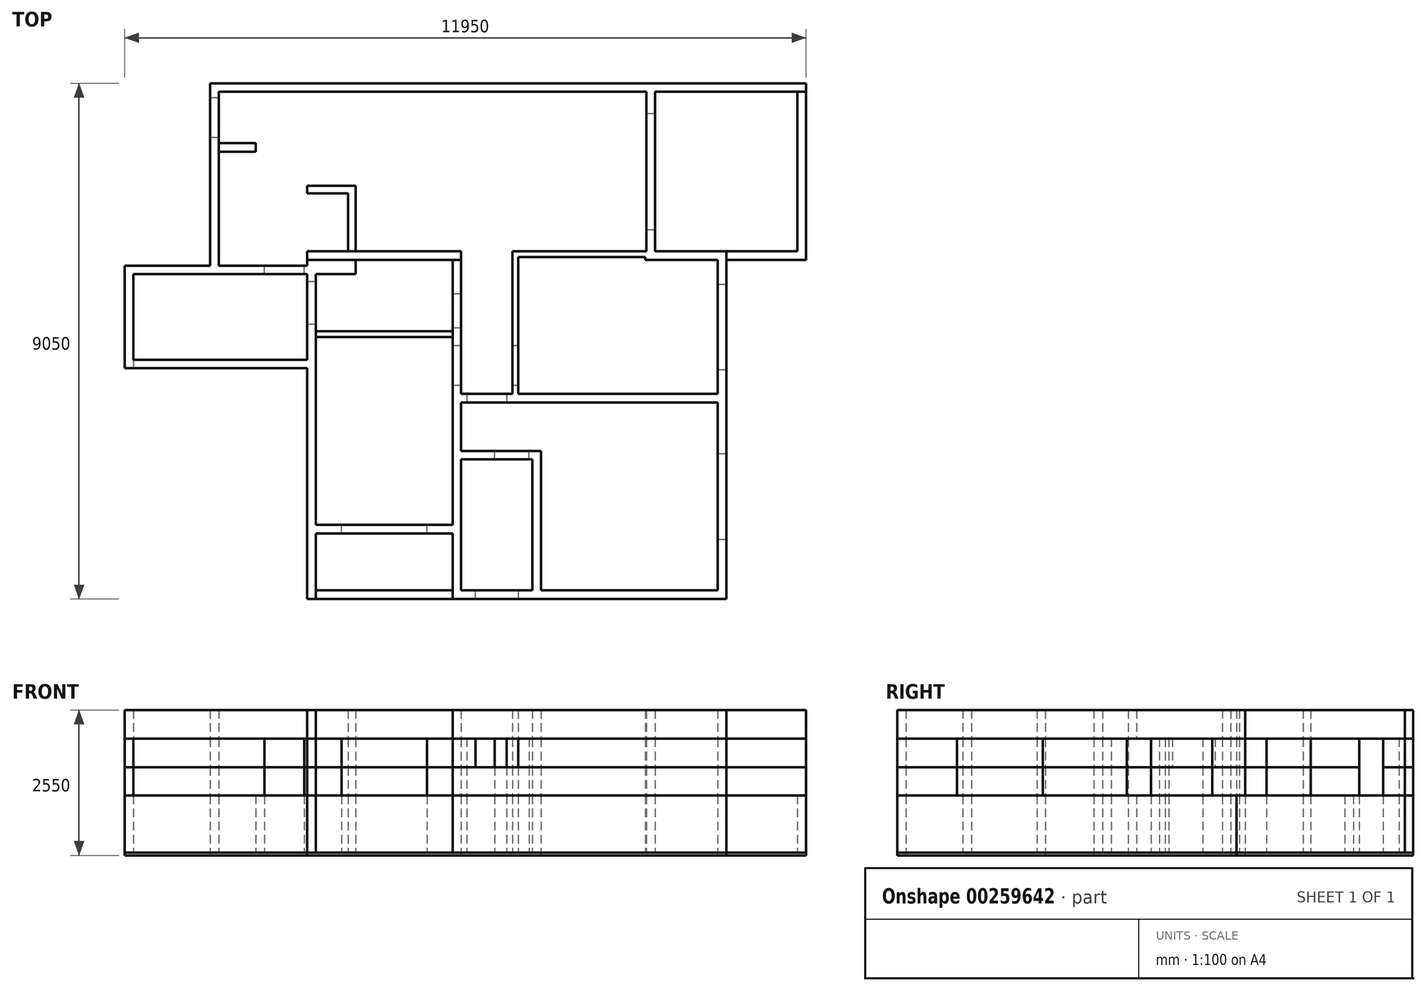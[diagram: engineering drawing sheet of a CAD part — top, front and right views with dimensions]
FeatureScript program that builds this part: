
annotation { "Feature Type Name" : "Feature", "Feature Type Description" : "" }
export const myFeature = defineFeature(function(context is Context, id is Id, definition is map)
    precondition{}
    {
        {
            var Q0;
            Q0=qCreatedBy(makeId("Top.planeOp"),FACE);
            var sketch = newSketch(context, id + "F0", { "sketchPlane" : qUnion([Q0])});
            skLineSegment(sketch, "E0.bottom", {"start": v(-5150, 2800) * mm, "end": v(2350, 2800) * mm});
            skLineSegment(sketch, "E0.top", {"start": v(-3600, 0) * mm, "end": v(-900, 0) * mm});
            skLineSegment(sketch, "E0.left", {"start": v(-5150, 2800) * mm, "end": v(-5150, 0) * mm});
            skLineSegment(sketch, "E0.right", {"start": v(5000, 2800) * mm, "end": v(5000, 0) * mm});
            skLineSegment(sketch, "E1.bottom", {"start": v(-5300, 2950) * mm, "end": v(5150, 2950) * mm});
            skLineSegment(sketch, "E1.top", {"start": v(-5300, -150) * mm, "end": v(-5150, -150) * mm});
            skLineSegment(sketch, "E1.left", {"start": v(-5300, 2950) * mm, "end": v(-5300, -150) * mm});
            skLineSegment(sketch, "E1.right", {"start": v(5150, 2950) * mm, "end": v(5150, -150) * mm});
            skLineSegment(sketch, "E2.top", {"start": v(2350, 2420) * mm, "end": v(2500, 2420) * mm});
            skLineSegment(sketch, "E2.left", {"start": v(2350, 2800) * mm, "end": v(2350, 2420) * mm});
            skLineSegment(sketch, "E2.right", {"start": v(2500, 2800) * mm, "end": v(2500, 2420) * mm});
            skLineSegment(sketch, "E3.top", {"start": v(2350, 380) * mm, "end": v(2500, 380) * mm});
            skLineSegment(sketch, "E3.left", {"start": v(2350, 2420) * mm, "end": v(2350, 380) * mm});
            skLineSegment(sketch, "E3.right", {"start": v(2500, 2420) * mm, "end": v(2500, 380) * mm});
            skLineSegment(sketch, "E4.left", {"start": v(2350, 380) * mm, "end": v(2350, 0) * mm});
            skLineSegment(sketch, "E4.right", {"start": v(2500, 380) * mm, "end": v(2500, 0) * mm});
            skLineSegment(sketch, "E5.bottom", {"start": v(0, 0) * mm, "end": v(2350, 0) * mm});
            skLineSegment(sketch, "E5.top", {"start": v(0, -2650) * mm, "end": v(3600, -2650) * mm});
            skLineSegment(sketch, "E5.left", {"start": v(0, 0) * mm, "end": v(0, -2650) * mm});
            skLineSegment(sketch, "E5.right", {"start": v(3750, 0) * mm, "end": v(3750, -2650) * mm});
            skLineSegment(sketch, "E6.bottom", {"start": v(100, -2500) * mm, "end": v(3600, -2500) * mm});
            skLineSegment(sketch, "E6.top", {"start": v(100, -100) * mm, "end": v(2330, -100) * mm});
            skLineSegment(sketch, "E6.left", {"start": v(100, -2500) * mm, "end": v(100, -100) * mm});
            skLineSegment(sketch, "E6.right", {"start": v(3600, -2500) * mm, "end": v(3600, -150) * mm});
            skLineSegment(sketch, "E7", {"start": v(2330, -100) * mm, "end": v(2330, -150) * mm});
            skLineSegment(sketch, "E8.trimOffspring", {"start": v(2330, -150) * mm, "end": v(3600, -150) * mm});
            skLineSegment(sketch, "E9.trimOffspring", {"start": v(2500, 2800) * mm, "end": v(5000, 2800) * mm});
            skLineSegment(sketch, "E10.trimOffspring", {"start": v(2500, 0) * mm, "end": v(3750, 0) * mm});
            skLineSegment(sketch, "E11.trimOffspring", {"start": v(2500, 0) * mm, "end": v(5000, 0) * mm});
            skLineSegment(sketch, "E12.trimOffspring", {"start": v(3750, -150) * mm, "end": v(5150, -150) * mm});
            skLineSegment(sketch, "E13.bottom", {"start": v(3600, -2500) * mm, "end": v(-1050, -2500) * mm});
            skLineSegment(sketch, "E13.top", {"start": v(3750, -6100) * mm, "end": v(-1050, -6100) * mm});
            skLineSegment(sketch, "E13.left", {"start": v(3750, -2500) * mm, "end": v(3750, -6100) * mm});
            skLineSegment(sketch, "E13.right", {"start": v(-1050, -2500) * mm, "end": v(-1050, -4800) * mm});
            skLineSegment(sketch, "E14.bottom", {"start": v(3600, -2650) * mm, "end": v(-900, -2650) * mm});
            skLineSegment(sketch, "E14.top", {"start": v(3600, -5950) * mm, "end": v(-900, -5950) * mm});
            skLineSegment(sketch, "E14.left", {"start": v(3600, -2650) * mm, "end": v(3600, -5950) * mm});
            skLineSegment(sketch, "E14.right", {"start": v(-900, -2650) * mm, "end": v(-900, -5950) * mm});
            skLineSegment(sketch, "E15.bottom", {"start": v(-900, -6100) * mm, "end": v(-3600, -6100) * mm});
            skLineSegment(sketch, "E15.top", {"start": v(-900, 0) * mm, "end": v(-3600, 0) * mm});
            skLineSegment(sketch, "E15.left", {"start": v(-900, -6100) * mm, "end": v(-900, 0) * mm});
            skLineSegment(sketch, "E15.right", {"start": v(-3600, -6100) * mm, "end": v(-3600, 0) * mm});
            skLineSegment(sketch, "E16.bottom", {"start": v(-1050, -5950) * mm, "end": v(-3450, -5950) * mm});
            skLineSegment(sketch, "E16.top", {"start": v(-1050, -150) * mm, "end": v(-3450, -150) * mm});
            skLineSegment(sketch, "E16.left", {"start": v(-1050, -5950) * mm, "end": v(-1050, -4950) * mm});
            skLineSegment(sketch, "E16.right", {"start": v(-3450, -5950) * mm, "end": v(-3450, -4950) * mm});
            skLineSegment(sketch, "E17.bottom", {"start": v(-1050, -1400) * mm, "end": v(-3450, -1400) * mm});
            skLineSegment(sketch, "E17.top", {"start": v(-1050, -1500) * mm, "end": v(-3450, -1500) * mm});
            skLineSegment(sketch, "E17.left", {"start": v(-1050, -1400) * mm, "end": v(-1050, -1500) * mm});
            skLineSegment(sketch, "E17.right", {"start": v(-3450, -1400) * mm, "end": v(-3450, -1500) * mm});
            skLineSegment(sketch, "E18.bottom", {"start": v(-3450, -4950) * mm, "end": v(-3000, -4950) * mm});
            skLineSegment(sketch, "E18.top", {"start": v(-3450, -4800) * mm, "end": v(-3000, -4800) * mm});
            skLineSegment(sketch, "E18.right", {"start": v(-3000, -4950) * mm, "end": v(-3000, -4800) * mm});
            skLineSegment(sketch, "E19.bottom", {"start": v(-3000, -4950) * mm, "end": v(-1500, -4950) * mm});
            skLineSegment(sketch, "E19.top", {"start": v(-3000, -4800) * mm, "end": v(-1500, -4800) * mm});
            skLineSegment(sketch, "E19.right", {"start": v(-1500, -4950) * mm, "end": v(-1500, -4800) * mm});
            skLineSegment(sketch, "E20.bottom", {"start": v(-1500, -4950) * mm, "end": v(-1050, -4950) * mm});
            skLineSegment(sketch, "E20.top", {"start": v(-1500, -4800) * mm, "end": v(-1050, -4800) * mm});
            skLineSegment(sketch, "E21.trimOffspring", {"start": v(-3450, -4800) * mm, "end": v(-3450, -150) * mm});
            skLineSegment(sketch, "E22.trimOffspring", {"start": v(-1050, -4950) * mm, "end": v(-1050, -6100) * mm});
            skLineSegment(sketch, "E23.trimOffspring", {"start": v(-1050, -4800) * mm, "end": v(-1050, -150) * mm});
            skLineSegment(sketch, "E24.trimOffspring", {"start": v(0, -150) * mm, "end": v(100, -150) * mm});
            skLineSegment(sketch, "E25.bottom", {"start": v(-5150, 1750) * mm, "end": v(-4500, 1750) * mm});
            skLineSegment(sketch, "E25.top", {"start": v(-5150, -250) * mm, "end": v(-2750, -250) * mm});
            skLineSegment(sketch, "E25.left", {"start": v(-5150, 1750) * mm, "end": v(-5150, -250) * mm});
            skLineSegment(sketch, "E25.right", {"start": v(-2750, 1750) * mm, "end": v(-2750, -250) * mm});
            skLineSegment(sketch, "E26.bottom", {"start": v(-5300, 1900) * mm, "end": v(-2750, 1900) * mm});
            skLineSegment(sketch, "E26.top", {"start": v(-5300, -400) * mm, "end": v(-2750, -400) * mm});
            skLineSegment(sketch, "E26.left", {"start": v(-5300, 1900) * mm, "end": v(-5300, -400) * mm});
            skLineSegment(sketch, "E26.right", {"start": v(-2750, 1900) * mm, "end": v(-2750, -400) * mm});
            skLineSegment(sketch, "E27", {"start": v(-4500, 1750) * mm, "end": v(-4500, 1900) * mm});
            skLineSegment(sketch, "E28.trimOffspring", {"start": v(-3600, -150) * mm, "end": v(-900, -150) * mm});
            skLineSegment(sketch, "E29.bottom", {"start": v(-3600, -400) * mm, "end": v(-6650, -400) * mm});
            skLineSegment(sketch, "E29.top", {"start": v(-3600, -1900) * mm, "end": v(-6650, -1900) * mm});
            skLineSegment(sketch, "E29.left", {"start": v(-3600, -400) * mm, "end": v(-3600, -1900) * mm});
            skLineSegment(sketch, "E29.right", {"start": v(-6650, -400) * mm, "end": v(-6650, -1900) * mm});
            skLineSegment(sketch, "E30.bottom", {"start": v(-3600, -400) * mm, "end": v(-6800, -400) * mm});
            skLineSegment(sketch, "E30.top", {"start": v(-3600, -2050) * mm, "end": v(-6800, -2050) * mm});
            skLineSegment(sketch, "E30.left", {"start": v(-3600, -400) * mm, "end": v(-3600, -2050) * mm});
            skLineSegment(sketch, "E30.right", {"start": v(-6800, -400) * mm, "end": v(-6800, -2050) * mm});
            skLineSegment(sketch, "E31", {"start": v(-2750, 1150) * mm, "end": v(-3600, 1150) * mm});
            skLineSegment(sketch, "E32", {"start": v(-3600, 1150) * mm, "end": v(-3600, 1020) * mm});
            skLineSegment(sketch, "E33", {"start": v(-3600, 1020) * mm, "end": v(-2880, 1020) * mm});
            skLineSegment(sketch, "E34", {"start": v(-2880, 1020) * mm, "end": v(-2880, 0) * mm});
            skLineSegment(sketch, "E35.bottom", {"start": v(-900, -5950) * mm, "end": v(350, -5950) * mm});
            skLineSegment(sketch, "E35.top", {"start": v(-900, -3650) * mm, "end": v(350, -3650) * mm});
            skLineSegment(sketch, "E35.left", {"start": v(-900, -5950) * mm, "end": v(-900, -3650) * mm});
            skLineSegment(sketch, "E35.right", {"start": v(350, -5950) * mm, "end": v(350, -3650) * mm});
            skLineSegment(sketch, "E36.bottom", {"start": v(-900, -5950) * mm, "end": v(500, -5950) * mm});
            skLineSegment(sketch, "E36.top", {"start": v(-900, -3500) * mm, "end": v(500, -3500) * mm});
            skLineSegment(sketch, "E36.left", {"start": v(-900, -5950) * mm, "end": v(-900, -3500) * mm});
            skLineSegment(sketch, "E36.right", {"start": v(500, -5950) * mm, "end": v(500, -3500) * mm});
            skLineSegment(sketch, "E37", {"start": v(2350, 0) * mm, "end": v(2350, -150) * mm});
            skLineSegment(sketch, "E38", {"start": v(5000, 2800) * mm, "end": v(5150, 2800) * mm});
            skLineSegment(sketch, "E39.bottom", {"start": v(-6800, -400) * mm, "end": v(-5300, -400) * mm});
            skLineSegment(sketch, "E39.top", {"start": v(-6800, -250) * mm, "end": v(-5300, -250) * mm});
            skLineSegment(sketch, "E39.left", {"start": v(-6800, -400) * mm, "end": v(-6800, -250) * mm});
            skLineSegment(sketch, "E39.right", {"start": v(-5300, -400) * mm, "end": v(-5300, -250) * mm});
            skLineSegment(sketch, "E40", {"start": v(-3450, -5950) * mm, "end": v(-3450, -6100) * mm});
            skLineSegment(sketch, "E41", {"start": v(-6650, -1900) * mm, "end": v(-6650, -2050) * mm});
            skLineSegment(sketch, "E42", {"start": v(3600, -5050) * mm, "end": v(3750, -5050) * mm});
            skLineSegment(sketch, "E43", {"start": v(3600, -3550) * mm, "end": v(3750, -3550) * mm});
            skLineSegment(sketch, "E44", {"start": v(3600, -575) * mm, "end": v(3750, -575) * mm});
            skLineSegment(sketch, "E45", {"start": v(3600, -2075) * mm, "end": v(3750, -2075) * mm});
            skLineSegment(sketch, "E46", {"start": v(3600, -4300) * mm, "end": v(3750, -4300) * mm, "construction": true});
            skLineSegment(sketch, "E47", {"start": v(3600, -1325) * mm, "end": v(3750, -1325) * mm, "construction": true});
            skLineSegment(sketch, "E48", {"start": v(-800, -2500) * mm, "end": v(-800, -2650) * mm});
            skLineSegment(sketch, "E49", {"start": v(-100, -2500) * mm, "end": v(-100, -2650) * mm});
            skLineSegment(sketch, "E50", {"start": v(-450, -2500) * mm, "end": v(-450, -2650) * mm, "construction": true});
            skLineSegment(sketch, "E51", {"start": v(290, -3650) * mm, "end": v(290, -3500) * mm});
            skLineSegment(sketch, "E52", {"start": v(-310, -3650) * mm, "end": v(-310, -3500) * mm});
            skLineSegment(sketch, "E53", {"start": v(-1050, -1650) * mm, "end": v(-900, -1650) * mm});
            skLineSegment(sketch, "E54", {"start": v(-1050, -2350) * mm, "end": v(-900, -2350) * mm});
            skLineSegment(sketch, "E55", {"start": v(-1050, -1340) * mm, "end": v(-900, -1340) * mm});
            skLineSegment(sketch, "E56", {"start": v(-1050, -740) * mm, "end": v(-900, -740) * mm});
            skLineSegment(sketch, "E57", {"start": v(-3600, -525) * mm, "end": v(-3450, -525) * mm});
            skLineSegment(sketch, "E58", {"start": v(-3600, -1275) * mm, "end": v(-3450, -1275) * mm});
            skLineSegment(sketch, "E59", {"start": v(-650, -6100) * mm, "end": v(-650, -5950) * mm});
            skLineSegment(sketch, "E60", {"start": v(-3600, -900) * mm, "end": v(-3450, -900) * mm, "construction": true});
            skLineSegment(sketch, "E61", {"start": v(-275, -5950) * mm, "end": v(-275, -6100) * mm, "construction": true});
            skLineSegment(sketch, "E62", {"start": v(100, -5950) * mm, "end": v(100, -6100) * mm});
            skLineSegment(sketch, "E63", {"start": v(-5300, 2000) * mm, "end": v(-5150, 2000) * mm});
            skLineSegment(sketch, "E64", {"start": v(-5300, 2700) * mm, "end": v(-5150, 2700) * mm});
            skLineSegment(sketch, "E65", {"start": v(-5300, 2350) * mm, "end": v(-5150, 2350) * mm, "construction": true});
            skLineSegment(sketch, "E66", {"start": v(0, -2350) * mm, "end": v(100, -2350) * mm});
            skLineSegment(sketch, "E67", {"start": v(0, -1650) * mm, "end": v(100, -1650) * mm});
            skLineSegment(sketch, "E68", {"start": v(-3650, -400) * mm, "end": v(-3650, -250) * mm});
            skLineSegment(sketch, "E69", {"start": v(-4350, -400) * mm, "end": v(-4350, -250) * mm});
            skLineSegment(sketch, "E70", {"start": v(-1050, -2000) * mm, "end": v(-900, -2000) * mm, "construction": true});
            skSolve(sketch);
        }
        {
            var Q0;
            {var subQ1=sQuery(id+"F0.wireOp",EDGE,"E14.top");Q0=makeQuery(id+"F0.imprint","IMPRINT",FACE,{"disambiguationData":[TD([[makeQuery(id+"F0.imprint","IMPRINT",EDGE,{"derivedFrom":subQ1}),1.0]])]});}
            var Q1;
            {var subQ0=sQuery(id+"F0.wireOp",EDGE,"E42");Q1=makeQuery(id+"F0.imprint","IMPRINT",FACE,{"disambiguationData":[TD([[makeQuery(id+"F0.imprint","IMPRINT",EDGE,{"derivedFrom":subQ0}),1.0]])]});}
            var Q2;
            {var subQ7=sQuery(id+"F0.wireOp",EDGE,"E43");Q2=makeQuery(id+"F0.imprint","IMPRINT",FACE,{"disambiguationData":[TD([[makeQuery(id+"F0.imprint","IMPRINT",EDGE,{"derivedFrom":subQ7}),1.0]])]});}
            var Q3;
            {var subQ1=sQuery(id+"F0.wireOp",EDGE,"E14.top");Q3=makeQuery(id+"F0.imprint","IMPRINT",FACE,{"disambiguationData":[TD([[makeQuery(id+"F0.imprint","IMPRINT",EDGE,{"derivedFrom":subQ1}),-1.0]])]});}
            var Q4;
            {var subQ3=sQuery(id+"F0.wireOp",EDGE,"E35.right");Q4=makeQuery(id+"F0.imprint","IMPRINT",FACE,{"disambiguationData":[TD([[makeQuery(id+"F0.imprint","IMPRINT",EDGE,{"derivedFrom":subQ3}),-1.0]])]});}
            var Q5;
            {var subQ0=sQuery(id+"F0.wireOp",EDGE,"E51");Q5=makeQuery(id+"F0.imprint","IMPRINT",FACE,{"disambiguationData":[TD([[makeQuery(id+"F0.imprint","IMPRINT",EDGE,{"derivedFrom":subQ0}),1.0]])]});}
            var Q6;
            {var subQ3=sQuery(id+"F0.wireOp",EDGE,"E52");Q6=makeQuery(id+"F0.imprint","IMPRINT",FACE,{"disambiguationData":[TD([[makeQuery(id+"F0.imprint","IMPRINT",EDGE,{"derivedFrom":subQ3}),1.0]])]});}
            var Q7;
            {var subQ0=sQuery(id+"F0.wireOp",EDGE,"E59");Q7=makeQuery(id+"F0.imprint","IMPRINT",FACE,{"disambiguationData":[TD([[makeQuery(id+"F0.imprint","IMPRINT",EDGE,{"derivedFrom":subQ0}),-1.0]])]});}
            var Q8;
            {var subQ3=sQuery(id+"F0.wireOp",EDGE,"E59");Q8=makeQuery(id+"F0.imprint","IMPRINT",FACE,{"disambiguationData":[TD([[makeQuery(id+"F0.imprint","IMPRINT",EDGE,{"derivedFrom":subQ3}),1.0]])]});}
            var Q9;
            {var subQ2=sQuery(id+"F0.wireOp",EDGE,"E20.bottom");Q9=makeQuery(id+"F0.imprint","IMPRINT",FACE,{"disambiguationData":[TD([[makeQuery(id+"F0.imprint","IMPRINT",EDGE,{"derivedFrom":subQ2}),1.0]])]});}
            var Q10;
            Q10=makeQuery(id+"F0.imprint","IMPRINT",FACE,{"disambiguationData":[TD([[makeQuery(id+"F0.imprint","IMPRINT",EDGE,{"derivedFrom":sQuery(id+"F0.wireOp",EDGE,"E19.bottom")}),1.0]])]});
            var Q11;
            Q11=makeQuery(id+"F0.imprint","IMPRINT",FACE,{"disambiguationData":[TD([[makeQuery(id+"F0.imprint","IMPRINT",EDGE,{"derivedFrom":sQuery(id+"F0.wireOp",EDGE,"E16.right")}),1.0]])]});
            var Q12;
            {var subQ4=sQuery(id+"F0.wireOp",EDGE,"E17.top");Q12=makeQuery(id+"F0.imprint","IMPRINT",FACE,{"disambiguationData":[TD([[makeQuery(id+"F0.imprint","IMPRINT",EDGE,{"derivedFrom":subQ4}),1.0]])]});}
            var Q13;
            {var subQ5=sQuery(id+"F0.wireOp",EDGE,"E54");Q13=makeQuery(id+"F0.imprint","IMPRINT",FACE,{"disambiguationData":[TD([[makeQuery(id+"F0.imprint","IMPRINT",EDGE,{"derivedFrom":subQ5}),-1.0]])]});}
            var Q14;
            {var subQ0=sQuery(id+"F0.wireOp",EDGE,"E48");Q14=makeQuery(id+"F0.imprint","IMPRINT",FACE,{"disambiguationData":[TD([[makeQuery(id+"F0.imprint","IMPRINT",EDGE,{"derivedFrom":subQ0}),-1.0]])]});}
            var Q15;
            {var subQ0=sQuery(id+"F0.wireOp",EDGE,"E48");Q15=makeQuery(id+"F0.imprint","IMPRINT",FACE,{"disambiguationData":[TD([[makeQuery(id+"F0.imprint","IMPRINT",EDGE,{"derivedFrom":subQ0}),1.0]])]});}
            var Q16;
            {var subQ5=sQuery(id+"F0.wireOp",EDGE,"E49");Q16=makeQuery(id+"F0.imprint","IMPRINT",FACE,{"disambiguationData":[TD([[makeQuery(id+"F0.imprint","IMPRINT",EDGE,{"derivedFrom":subQ5}),1.0]])]});}
            var Q17;
            {var subQ0=sQuery(id+"F0.wireOp",EDGE,"E53");Q17=makeQuery(id+"F0.imprint","IMPRINT",FACE,{"disambiguationData":[TD([[makeQuery(id+"F0.imprint","IMPRINT",EDGE,{"derivedFrom":subQ0}),-1.0]])]});}
            var Q18;
            {var subQ4=sQuery(id+"F0.wireOp",EDGE,"E53");Q18=makeQuery(id+"F0.imprint","IMPRINT",FACE,{"disambiguationData":[TD([[makeQuery(id+"F0.imprint","IMPRINT",EDGE,{"derivedFrom":subQ4}),1.0]])]});}
            var Q19;
            {var subQ0=sQuery(id+"F0.wireOp",EDGE,"E55");Q19=makeQuery(id+"F0.imprint","IMPRINT",FACE,{"disambiguationData":[TD([[makeQuery(id+"F0.imprint","IMPRINT",EDGE,{"derivedFrom":subQ0}),1.0]])]});}
            var Q20;
            {var subQ0=sQuery(id+"F0.wireOp",EDGE,"E17.bottom");Q20=makeQuery(id+"F0.imprint","IMPRINT",FACE,{"disambiguationData":[TD([[makeQuery(id+"F0.imprint","IMPRINT",EDGE,{"derivedFrom":subQ0}),1.0]])]});}
            var Q21;
            {var subQ3=sQuery(id+"F0.wireOp",EDGE,"E56");Q21=makeQuery(id+"F0.imprint","IMPRINT",FACE,{"disambiguationData":[TD([[makeQuery(id+"F0.imprint","IMPRINT",EDGE,{"derivedFrom":subQ3}),1.0]])]});}
            var Q22;
            {var subQ1=sQuery(id+"F0.wireOp",EDGE,"E15.top");var subQ5=sQuery(id+"F0.wireOp",EDGE,"E15.left");var subQ6=makeQuery(id+"F0.imprint","INTERSECT",VERTEX,{"derivedFrom":[subQ1,subQ5]});Q22=makeQuery(id+"F0.imprint","IMPRINT",FACE,{"disambiguationData":[TD([[makeQuery(id+"F0.imprint","IMPRINT",EDGE,{"disambiguationData":[TD([[subQ6,-1.0]])],"derivedFrom":subQ1}),1.0]])]});}
            var Q23;
            {var subQ0=sQuery(id+"F0.wireOp",EDGE,"E57");Q23=makeQuery(id+"F0.imprint","IMPRINT",FACE,{"disambiguationData":[TD([[makeQuery(id+"F0.imprint","IMPRINT",EDGE,{"derivedFrom":subQ0}),-1.0]])]});}
            var Q24;
            {var subQ0=sQuery(id+"F0.wireOp",EDGE,"E57");Q24=makeQuery(id+"F0.imprint","IMPRINT",FACE,{"disambiguationData":[TD([[makeQuery(id+"F0.imprint","IMPRINT",EDGE,{"derivedFrom":subQ0}),1.0]])]});}
            var Q25;
            {var subQ0=sQuery(id+"F0.wireOp",EDGE,"E26.top");var subQ5=sQuery(id+"F0.wireOp",EDGE,"E21.trimOffspring");var subQ6=makeQuery(id+"F0.imprint","INTERSECT",VERTEX,{"derivedFrom":[subQ5,subQ0]});Q25=makeQuery(id+"F0.imprint","IMPRINT",FACE,{"disambiguationData":[TD([[makeQuery(id+"F0.imprint","IMPRINT",EDGE,{"disambiguationData":[TD([[subQ6,-1.0]])],"derivedFrom":subQ5}),1.0]])]});}
            var Q26;
            {var subQ0=sQuery(id+"F0.wireOp",EDGE,"E26.top");var subQ1=sQuery(id+"F0.wireOp",EDGE,"E21.trimOffspring");var subQ2=makeQuery(id+"F0.imprint","INTERSECT",VERTEX,{"derivedFrom":[subQ1,subQ0]});Q26=makeQuery(id+"F0.imprint","IMPRINT",FACE,{"disambiguationData":[TD([[makeQuery(id+"F0.imprint","IMPRINT",EDGE,{"disambiguationData":[TD([[subQ2,-1.0]])],"derivedFrom":subQ1}),-1.0]])]});}
            var Q27;
            {var subQ0=sQuery(id+"F0.wireOp",EDGE,"E28.trimOffspring");var subQ1=sQuery(id+"F0.wireOp",EDGE,"E21.trimOffspring");var subQ2=makeQuery(id+"F0.imprint","INTERSECT",VERTEX,{"derivedFrom":[subQ1,subQ0]});Q27=makeQuery(id+"F0.imprint","IMPRINT",FACE,{"disambiguationData":[TD([[makeQuery(id+"F0.imprint","IMPRINT",EDGE,{"disambiguationData":[TD([[subQ2,1.0]])],"derivedFrom":subQ1}),-1.0]])]});}
            var Q28;
            {var subQ1=sQuery(id+"F0.wireOp",EDGE,"E15.top");var subQ8=makeQuery(id+"F0.imprint","INTERSECT",VERTEX,{"derivedFrom":[subQ1,sQuery(id+"F0.wireOp",EDGE,"E34")]});Q28=makeQuery(id+"F0.imprint","IMPRINT",FACE,{"disambiguationData":[TD([[makeQuery(id+"F0.imprint","IMPRINT",EDGE,{"disambiguationData":[TD([[subQ8,1.0]])],"derivedFrom":subQ1}),1.0]])]});}
            var Q29;
            {var subQ0=sQuery(id+"F0.wireOp",EDGE,"E28.trimOffspring");var subQ1=sQuery(id+"F0.wireOp",EDGE,"E15.right");var subQ2=makeQuery(id+"F0.imprint","INTERSECT",VERTEX,{"derivedFrom":[subQ1,subQ0]});Q29=makeQuery(id+"F0.imprint","IMPRINT",FACE,{"disambiguationData":[TD([[makeQuery(id+"F0.imprint","IMPRINT",EDGE,{"disambiguationData":[TD([[subQ2,1.0]])],"derivedFrom":subQ1}),-1.0]])]});}
            var Q30;
            {var subQ1=sQuery(id+"F0.wireOp",EDGE,"E1.top");Q30=makeQuery(id+"F0.imprint","IMPRINT",FACE,{"disambiguationData":[TD([[makeQuery(id+"F0.imprint","IMPRINT",EDGE,{"derivedFrom":subQ1}),-1.0]])]});}
            var Q31;
            Q31=makeQuery(id+"F0.imprint","IMPRINT",FACE,{"disambiguationData":[TD([[makeQuery(id+"F0.imprint","IMPRINT",EDGE,{"derivedFrom":sQuery(id+"F0.wireOp",EDGE,"E39.top")}),-1.0]])]});
            var Q32;
            {var subQ1=sQuery(id+"F0.wireOp",EDGE,"E29.right");Q32=makeQuery(id+"F0.imprint","IMPRINT",FACE,{"disambiguationData":[TD([[makeQuery(id+"F0.imprint","IMPRINT",EDGE,{"derivedFrom":subQ1}),-1.0]])]});}
            var Q33;
            {var subQ1=sQuery(id+"F0.wireOp",EDGE,"E1.top");Q33=makeQuery(id+"F0.imprint","IMPRINT",FACE,{"disambiguationData":[TD([[makeQuery(id+"F0.imprint","IMPRINT",EDGE,{"derivedFrom":subQ1}),1.0]])]});}
            var Q34;
            {var subQ0=sQuery(id+"F0.wireOp",EDGE,"E63");Q34=makeQuery(id+"F0.imprint","IMPRINT",FACE,{"disambiguationData":[TD([[makeQuery(id+"F0.imprint","IMPRINT",EDGE,{"derivedFrom":subQ0}),-1.0]])]});}
            var Q35;
            {var subQ0=sQuery(id+"F0.wireOp",EDGE,"E63");Q35=makeQuery(id+"F0.imprint","IMPRINT",FACE,{"disambiguationData":[TD([[makeQuery(id+"F0.imprint","IMPRINT",EDGE,{"derivedFrom":subQ0}),1.0]])]});}
            var Q36;
            {var subQ5=sQuery(id+"F0.wireOp",EDGE,"E0.bottom");Q36=makeQuery(id+"F0.imprint","IMPRINT",FACE,{"disambiguationData":[TD([[makeQuery(id+"F0.imprint","IMPRINT",EDGE,{"derivedFrom":subQ5}),1.0]])]});}
            var Q37;
            Q37=makeQuery(id+"F0.imprint","IMPRINT",FACE,{"disambiguationData":[TD([[makeQuery(id+"F0.imprint","IMPRINT",EDGE,{"derivedFrom":sQuery(id+"F0.wireOp",EDGE,"E2.top")}),-1.0]])]});
            var Q38;
            {var subQ0=sQuery(id+"F0.wireOp",EDGE,"E44");Q38=makeQuery(id+"F0.imprint","IMPRINT",FACE,{"disambiguationData":[TD([[makeQuery(id+"F0.imprint","IMPRINT",EDGE,{"derivedFrom":subQ0}),-1.0]])]});}
            var Q39;
            Q39=makeQuery(id+"F0.imprint","IMPRINT",FACE,{"disambiguationData":[TD([[makeQuery(id+"F0.imprint","IMPRINT",EDGE,{"derivedFrom":sQuery(id+"F0.wireOp",EDGE,"E3.top")}),-1.0]])]});
            var Q40;
            {var subQ0=sQuery(id+"F0.wireOp",EDGE,"E35.right");Q40=makeQuery(id+"F0.imprint","IMPRINT",FACE,{"disambiguationData":[TD([[makeQuery(id+"F0.imprint","IMPRINT",EDGE,{"derivedFrom":subQ0}),1.0]])]});}
            var Q41;
            {var subQ0=sQuery(id+"F0.wireOp",EDGE,"E16.bottom");Q41=makeQuery(id+"F0.imprint","IMPRINT",FACE,{"disambiguationData":[TD([[makeQuery(id+"F0.imprint","IMPRINT",EDGE,{"derivedFrom":subQ0}),-1.0]])]});}
            var Q42;
            {var subQ4=sQuery(id+"F0.wireOp",EDGE,"E16.bottom");Q42=makeQuery(id+"F0.imprint","IMPRINT",FACE,{"disambiguationData":[TD([[makeQuery(id+"F0.imprint","IMPRINT",EDGE,{"derivedFrom":subQ4}),1.0]])]});}
            var Q43;
            {var subQ4=sQuery(id+"F0.wireOp",EDGE,"E29.top");Q43=makeQuery(id+"F0.imprint","IMPRINT",FACE,{"disambiguationData":[TD([[makeQuery(id+"F0.imprint","IMPRINT",EDGE,{"derivedFrom":subQ4}),-1.0]])]});}
            var Q44;
            {var subQ0=sQuery(id+"F0.wireOp",EDGE,"E29.top");Q44=makeQuery(id+"F0.imprint","IMPRINT",FACE,{"disambiguationData":[TD([[makeQuery(id+"F0.imprint","IMPRINT",EDGE,{"derivedFrom":subQ0}),1.0]])]});}
            var Q45;
            {var subQ11=sQuery(id+"F0.wireOp",EDGE,"E17.bottom");Q45=makeQuery(id+"F0.imprint","IMPRINT",FACE,{"disambiguationData":[TD([[makeQuery(id+"F0.imprint","IMPRINT",EDGE,{"derivedFrom":subQ11}),-1.0]])]});}
            var Q46;
            {var subQ10=sQuery(id+"F0.wireOp",EDGE,"E6.top");Q46=makeQuery(id+"F0.imprint","IMPRINT",FACE,{"disambiguationData":[TD([[makeQuery(id+"F0.imprint","IMPRINT",EDGE,{"derivedFrom":subQ10}),-1.0]])]});}
            var Q47;
            {var subQ20=sQuery(id+"F0.wireOp",EDGE,"E0.bottom");Q47=makeQuery(id+"F0.imprint","IMPRINT",FACE,{"disambiguationData":[TD([[makeQuery(id+"F0.imprint","IMPRINT",EDGE,{"derivedFrom":subQ20}),-1.0]])]});}
            var Q48;
            {var subQ0=sQuery(id+"F0.wireOp",EDGE,"E66");Q48=makeQuery(id+"F0.imprint","IMPRINT",FACE,{"disambiguationData":[TD([[makeQuery(id+"F0.imprint","IMPRINT",EDGE,{"derivedFrom":subQ0}),-1.0]])]});}
            var Q49;
            {var subQ0=sQuery(id+"F0.wireOp",EDGE,"E66");Q49=makeQuery(id+"F0.imprint","IMPRINT",FACE,{"disambiguationData":[TD([[makeQuery(id+"F0.imprint","IMPRINT",EDGE,{"derivedFrom":subQ0}),1.0]])]});}
            var Q50;
            {var subQ0=sQuery(id+"F0.wireOp",EDGE,"E24.trimOffspring");Q50=makeQuery(id+"F0.imprint","IMPRINT",FACE,{"disambiguationData":[TD([[makeQuery(id+"F0.imprint","IMPRINT",EDGE,{"derivedFrom":subQ0}),-1.0]])]});}
            var Q51;
            {var subQ2=sQuery(id+"F0.wireOp",EDGE,"E6.top");Q51=makeQuery(id+"F0.imprint","IMPRINT",FACE,{"disambiguationData":[TD([[makeQuery(id+"F0.imprint","IMPRINT",EDGE,{"derivedFrom":subQ2}),1.0]])]});}
            var Q52;
            {var subQ3=sQuery(id+"F0.wireOp",EDGE,"E0.right");Q52=makeQuery(id+"F0.imprint","IMPRINT",FACE,{"disambiguationData":[TD([[makeQuery(id+"F0.imprint","IMPRINT",EDGE,{"derivedFrom":subQ3}),-1.0]])]});}
            var Q53;
            {var subQ1=sQuery(id+"F0.wireOp",EDGE,"E0.right");Q53=makeQuery(id+"F0.imprint","IMPRINT",FACE,{"disambiguationData":[TD([[makeQuery(id+"F0.imprint","IMPRINT",EDGE,{"derivedFrom":subQ1}),1.0]])]});}
            var Q54;
            {var subQ14=sQuery(id+"F0.wireOp",EDGE,"E25.bottom");Q54=makeQuery(id+"F0.imprint","IMPRINT",FACE,{"disambiguationData":[TD([[makeQuery(id+"F0.imprint","IMPRINT",EDGE,{"derivedFrom":subQ14}),-1.0]])]});}
            var Q55;
            {var subQ0=sQuery(id+"F0.wireOp",EDGE,"E25.bottom");Q55=makeQuery(id+"F0.imprint","IMPRINT",FACE,{"disambiguationData":[TD([[makeQuery(id+"F0.imprint","IMPRINT",EDGE,{"derivedFrom":subQ0}),1.0]])]});}
            var Q56;
            {var subQ0=sQuery(id+"F0.wireOp",EDGE,"E31");Q56=makeQuery(id+"F0.imprint","IMPRINT",FACE,{"disambiguationData":[TD([[makeQuery(id+"F0.imprint","IMPRINT",EDGE,{"derivedFrom":subQ0}),1.0]])]});}
            var Q57;
            {var subQ0=sQuery(id+"F0.wireOp",EDGE,"E68");Q57=makeQuery(id+"F0.imprint","IMPRINT",FACE,{"disambiguationData":[TD([[makeQuery(id+"F0.imprint","IMPRINT",EDGE,{"derivedFrom":subQ0}),1.0]])]});}
            var Q58;
            {var subQ5=sQuery(id+"F0.wireOp",EDGE,"E68");Q58=makeQuery(id+"F0.imprint","IMPRINT",FACE,{"disambiguationData":[TD([[makeQuery(id+"F0.imprint","IMPRINT",EDGE,{"derivedFrom":subQ5}),-1.0]])]});}
            extrude(context, id + "F1", {"entities" : qUnion([Q0, Q1, Q2, Q3, Q4, Q5, Q6, Q7, Q8, Q9, Q10, Q11, Q12, Q13, Q14, Q15, Q16, Q17, Q18, Q19, Q20, Q21, Q22, Q23, Q24, Q25, Q26, Q27, Q28, Q29, Q30, Q31, Q32, Q33, Q34, Q35, Q36, Q37, Q38, Q39, Q40, Q41, Q42, Q43, Q44, Q45, Q46, Q47, Q48, Q49, Q50, Q51, Q52, Q53, Q54, Q55, Q56, Q57, Q58]), "oppositeDirection" : true, "depth" : 50 * mm});
        }
        {
            var Q0;
            {var subQ1=sQuery(id+"F0.wireOp",EDGE,"E14.top");Q0=makeQuery(id+"F0.imprint","IMPRINT",FACE,{"disambiguationData":[TD([[makeQuery(id+"F0.imprint","IMPRINT",EDGE,{"derivedFrom":subQ1}),1.0]])]});}
            var Q1;
            {var subQ0=sQuery(id+"F0.wireOp",EDGE,"E42");Q1=makeQuery(id+"F0.imprint","IMPRINT",FACE,{"disambiguationData":[TD([[makeQuery(id+"F0.imprint","IMPRINT",EDGE,{"derivedFrom":subQ0}),1.0]])]});}
            var Q2;
            {var subQ7=sQuery(id+"F0.wireOp",EDGE,"E43");Q2=makeQuery(id+"F0.imprint","IMPRINT",FACE,{"disambiguationData":[TD([[makeQuery(id+"F0.imprint","IMPRINT",EDGE,{"derivedFrom":subQ7}),1.0]])]});}
            var Q3;
            {var subQ0=sQuery(id+"F0.wireOp",EDGE,"E44");Q3=makeQuery(id+"F0.imprint","IMPRINT",FACE,{"disambiguationData":[TD([[makeQuery(id+"F0.imprint","IMPRINT",EDGE,{"derivedFrom":subQ0}),-1.0]])]});}
            var Q4;
            Q4=makeQuery(id+"F0.imprint","IMPRINT",FACE,{"disambiguationData":[TD([[makeQuery(id+"F0.imprint","IMPRINT",EDGE,{"derivedFrom":sQuery(id+"F0.wireOp",EDGE,"E3.top")}),-1.0]])]});
            var Q5;
            {var subQ4=sQuery(id+"F0.wireOp",EDGE,"E0.bottom");Q5=makeQuery(id+"F0.imprint","IMPRINT",FACE,{"disambiguationData":[TD([[makeQuery(id+"F0.imprint","IMPRINT",EDGE,{"derivedFrom":subQ4}),1.0]])]});}
            var Q6;
            {var subQ3=sQuery(id+"F0.wireOp",EDGE,"E35.right");Q6=makeQuery(id+"F0.imprint","IMPRINT",FACE,{"disambiguationData":[TD([[makeQuery(id+"F0.imprint","IMPRINT",EDGE,{"derivedFrom":subQ3}),-1.0]])]});}
            var Q7;
            {var subQ3=sQuery(id+"F0.wireOp",EDGE,"E52");Q7=makeQuery(id+"F0.imprint","IMPRINT",FACE,{"disambiguationData":[TD([[makeQuery(id+"F0.imprint","IMPRINT",EDGE,{"derivedFrom":subQ3}),1.0]])]});}
            var Q8;
            {var subQ2=sQuery(id+"F0.wireOp",EDGE,"E20.bottom");Q8=makeQuery(id+"F0.imprint","IMPRINT",FACE,{"disambiguationData":[TD([[makeQuery(id+"F0.imprint","IMPRINT",EDGE,{"derivedFrom":subQ2}),1.0]])]});}
            var Q9;
            {var subQ0=sQuery(id+"F0.wireOp",EDGE,"E59");Q9=makeQuery(id+"F0.imprint","IMPRINT",FACE,{"disambiguationData":[TD([[makeQuery(id+"F0.imprint","IMPRINT",EDGE,{"derivedFrom":subQ0}),-1.0]])]});}
            var Q10;
            {var subQ3=sQuery(id+"F0.wireOp",EDGE,"E59");Q10=makeQuery(id+"F0.imprint","IMPRINT",FACE,{"disambiguationData":[TD([[makeQuery(id+"F0.imprint","IMPRINT",EDGE,{"derivedFrom":subQ3}),1.0]])]});}
            var Q11;
            Q11=makeQuery(id+"F0.imprint","IMPRINT",FACE,{"disambiguationData":[TD([[makeQuery(id+"F0.imprint","IMPRINT",EDGE,{"derivedFrom":sQuery(id+"F0.wireOp",EDGE,"E16.right")}),1.0]])]});
            var Q12;
            {var subQ0=sQuery(id+"F0.wireOp",EDGE,"E48");Q12=makeQuery(id+"F0.imprint","IMPRINT",FACE,{"disambiguationData":[TD([[makeQuery(id+"F0.imprint","IMPRINT",EDGE,{"derivedFrom":subQ0}),-1.0]])]});}
            var Q13;
            {var subQ5=sQuery(id+"F0.wireOp",EDGE,"E54");Q13=makeQuery(id+"F0.imprint","IMPRINT",FACE,{"disambiguationData":[TD([[makeQuery(id+"F0.imprint","IMPRINT",EDGE,{"derivedFrom":subQ5}),-1.0]])]});}
            var Q14;
            {var subQ4=sQuery(id+"F0.wireOp",EDGE,"E53");Q14=makeQuery(id+"F0.imprint","IMPRINT",FACE,{"disambiguationData":[TD([[makeQuery(id+"F0.imprint","IMPRINT",EDGE,{"derivedFrom":subQ4}),1.0]])]});}
            var Q15;
            {var subQ0=sQuery(id+"F0.wireOp",EDGE,"E17.bottom");Q15=makeQuery(id+"F0.imprint","IMPRINT",FACE,{"disambiguationData":[TD([[makeQuery(id+"F0.imprint","IMPRINT",EDGE,{"derivedFrom":subQ0}),1.0]])]});}
            var Q16;
            {var subQ0=sQuery(id+"F0.wireOp",EDGE,"E57");Q16=makeQuery(id+"F0.imprint","IMPRINT",FACE,{"disambiguationData":[TD([[makeQuery(id+"F0.imprint","IMPRINT",EDGE,{"derivedFrom":subQ0}),-1.0]])]});}
            var Q17;
            {var subQ0=sQuery(id+"F0.wireOp",EDGE,"E57");Q17=makeQuery(id+"F0.imprint","IMPRINT",FACE,{"disambiguationData":[TD([[makeQuery(id+"F0.imprint","IMPRINT",EDGE,{"derivedFrom":subQ0}),1.0]])]});}
            var Q18;
            {var subQ0=sQuery(id+"F0.wireOp",EDGE,"E26.top");var subQ5=sQuery(id+"F0.wireOp",EDGE,"E21.trimOffspring");var subQ6=makeQuery(id+"F0.imprint","INTERSECT",VERTEX,{"derivedFrom":[subQ5,subQ0]});Q18=makeQuery(id+"F0.imprint","IMPRINT",FACE,{"disambiguationData":[TD([[makeQuery(id+"F0.imprint","IMPRINT",EDGE,{"disambiguationData":[TD([[subQ6,-1.0]])],"derivedFrom":subQ5}),1.0]])]});}
            var Q19;
            {var subQ0=sQuery(id+"F0.wireOp",EDGE,"E26.top");var subQ1=sQuery(id+"F0.wireOp",EDGE,"E21.trimOffspring");var subQ2=makeQuery(id+"F0.imprint","INTERSECT",VERTEX,{"derivedFrom":[subQ1,subQ0]});Q19=makeQuery(id+"F0.imprint","IMPRINT",FACE,{"disambiguationData":[TD([[makeQuery(id+"F0.imprint","IMPRINT",EDGE,{"disambiguationData":[TD([[subQ2,-1.0]])],"derivedFrom":subQ1}),-1.0]])]});}
            var Q20;
            {var subQ0=sQuery(id+"F0.wireOp",EDGE,"E28.trimOffspring");var subQ1=sQuery(id+"F0.wireOp",EDGE,"E21.trimOffspring");var subQ2=makeQuery(id+"F0.imprint","INTERSECT",VERTEX,{"derivedFrom":[subQ1,subQ0]});Q20=makeQuery(id+"F0.imprint","IMPRINT",FACE,{"disambiguationData":[TD([[makeQuery(id+"F0.imprint","IMPRINT",EDGE,{"disambiguationData":[TD([[subQ2,1.0]])],"derivedFrom":subQ1}),-1.0]])]});}
            var Q21;
            {var subQ1=sQuery(id+"F0.wireOp",EDGE,"E15.top");var subQ6=makeQuery(id+"F0.imprint","INTERSECT",VERTEX,{"derivedFrom":[subQ1,sQuery(id+"F0.wireOp",EDGE,"E34")]});Q21=makeQuery(id+"F0.imprint","IMPRINT",FACE,{"disambiguationData":[TD([[makeQuery(id+"F0.imprint","IMPRINT",EDGE,{"disambiguationData":[TD([[subQ6,1.0]])],"derivedFrom":subQ1}),1.0]])]});}
            var Q22;
            {var subQ0=sQuery(id+"F0.wireOp",EDGE,"E28.trimOffspring");var subQ1=sQuery(id+"F0.wireOp",EDGE,"E15.right");var subQ2=makeQuery(id+"F0.imprint","INTERSECT",VERTEX,{"derivedFrom":[subQ1,subQ0]});Q22=makeQuery(id+"F0.imprint","IMPRINT",FACE,{"disambiguationData":[TD([[makeQuery(id+"F0.imprint","IMPRINT",EDGE,{"disambiguationData":[TD([[subQ2,1.0]])],"derivedFrom":subQ1}),-1.0]])]});}
            var Q23;
            {var subQ5=sQuery(id+"F0.wireOp",EDGE,"E68");Q23=makeQuery(id+"F0.imprint","IMPRINT",FACE,{"disambiguationData":[TD([[makeQuery(id+"F0.imprint","IMPRINT",EDGE,{"derivedFrom":subQ5}),-1.0]])]});}
            var Q24;
            {var subQ1=sQuery(id+"F0.wireOp",EDGE,"E1.top");Q24=makeQuery(id+"F0.imprint","IMPRINT",FACE,{"disambiguationData":[TD([[makeQuery(id+"F0.imprint","IMPRINT",EDGE,{"derivedFrom":subQ1}),-1.0]])]});}
            var Q25;
            Q25=makeQuery(id+"F0.imprint","IMPRINT",FACE,{"disambiguationData":[TD([[makeQuery(id+"F0.imprint","IMPRINT",EDGE,{"derivedFrom":sQuery(id+"F0.wireOp",EDGE,"E39.top")}),-1.0]])]});
            var Q26;
            {var subQ0=sQuery(id+"F0.wireOp",EDGE,"E29.top");Q26=makeQuery(id+"F0.imprint","IMPRINT",FACE,{"disambiguationData":[TD([[makeQuery(id+"F0.imprint","IMPRINT",EDGE,{"derivedFrom":subQ0}),1.0]])]});}
            var Q27;
            {var subQ1=sQuery(id+"F0.wireOp",EDGE,"E29.right");Q27=makeQuery(id+"F0.imprint","IMPRINT",FACE,{"disambiguationData":[TD([[makeQuery(id+"F0.imprint","IMPRINT",EDGE,{"derivedFrom":subQ1}),-1.0]])]});}
            var Q28;
            {var subQ4=sQuery(id+"F0.wireOp",EDGE,"E1.top");Q28=makeQuery(id+"F0.imprint","IMPRINT",FACE,{"disambiguationData":[TD([[makeQuery(id+"F0.imprint","IMPRINT",EDGE,{"derivedFrom":subQ4}),1.0]])]});}
            var Q29;
            {var subQ0=sQuery(id+"F0.wireOp",EDGE,"E25.bottom");Q29=makeQuery(id+"F0.imprint","IMPRINT",FACE,{"disambiguationData":[TD([[makeQuery(id+"F0.imprint","IMPRINT",EDGE,{"derivedFrom":subQ0}),1.0]])]});}
            var Q30;
            {var subQ0=sQuery(id+"F0.wireOp",EDGE,"E63");Q30=makeQuery(id+"F0.imprint","IMPRINT",FACE,{"disambiguationData":[TD([[makeQuery(id+"F0.imprint","IMPRINT",EDGE,{"derivedFrom":subQ0}),-1.0]])]});}
            var Q31;
            {var subQ0=sQuery(id+"F0.wireOp",EDGE,"E31");Q31=makeQuery(id+"F0.imprint","IMPRINT",FACE,{"disambiguationData":[TD([[makeQuery(id+"F0.imprint","IMPRINT",EDGE,{"derivedFrom":subQ0}),1.0]])]});}
            var Q32;
            {var subQ3=sQuery(id+"F0.wireOp",EDGE,"E56");Q32=makeQuery(id+"F0.imprint","IMPRINT",FACE,{"disambiguationData":[TD([[makeQuery(id+"F0.imprint","IMPRINT",EDGE,{"derivedFrom":subQ3}),1.0]])]});}
            var Q33;
            {var subQ4=sQuery(id+"F0.wireOp",EDGE,"E15.top");var subQ6=sQuery(id+"F0.wireOp",EDGE,"E15.left");var subQ7=makeQuery(id+"F0.imprint","INTERSECT",VERTEX,{"derivedFrom":[subQ4,subQ6]});Q33=makeQuery(id+"F0.imprint","IMPRINT",FACE,{"disambiguationData":[TD([[makeQuery(id+"F0.imprint","IMPRINT",EDGE,{"disambiguationData":[TD([[subQ7,-1.0]])],"derivedFrom":subQ4}),1.0]])]});}
            var Q34;
            {var subQ5=sQuery(id+"F0.wireOp",EDGE,"E49");Q34=makeQuery(id+"F0.imprint","IMPRINT",FACE,{"disambiguationData":[TD([[makeQuery(id+"F0.imprint","IMPRINT",EDGE,{"derivedFrom":subQ5}),1.0]])]});}
            var Q35;
            {var subQ2=sQuery(id+"F0.wireOp",EDGE,"E6.top");Q35=makeQuery(id+"F0.imprint","IMPRINT",FACE,{"disambiguationData":[TD([[makeQuery(id+"F0.imprint","IMPRINT",EDGE,{"derivedFrom":subQ2}),1.0]])]});}
            var Q36;
            {var subQ0=sQuery(id+"F0.wireOp",EDGE,"E24.trimOffspring");Q36=makeQuery(id+"F0.imprint","IMPRINT",FACE,{"disambiguationData":[TD([[makeQuery(id+"F0.imprint","IMPRINT",EDGE,{"derivedFrom":subQ0}),-1.0]])]});}
            var Q37;
            {var subQ0=sQuery(id+"F0.wireOp",EDGE,"E66");Q37=makeQuery(id+"F0.imprint","IMPRINT",FACE,{"disambiguationData":[TD([[makeQuery(id+"F0.imprint","IMPRINT",EDGE,{"derivedFrom":subQ0}),-1.0]])]});}
            extrude(context, id + "F2", {"entities" : qUnion([Q0, Q1, Q2, Q3, Q4, Q5, Q6, Q7, Q8, Q9, Q10, Q11, Q12, Q13, Q14, Q15, Q16, Q17, Q18, Q19, Q20, Q21, Q22, Q23, Q24, Q25, Q26, Q27, Q28, Q29, Q30, Q31, Q32, Q33, Q34, Q35, Q36, Q37]), "depth" : 1000 * mm});
        }
        {
            var Q0;
            {var subQ2=sQuery(id+"F0.wireOp",EDGE,"E20.bottom");Q0=makeQuery(id+"F0.imprint","IMPRINT",FACE,{"disambiguationData":[TD([[makeQuery(id+"F0.imprint","IMPRINT",EDGE,{"derivedFrom":subQ2}),1.0]])]});}
            var Q1;
            {var subQ3=sQuery(id+"F0.wireOp",EDGE,"E59");Q1=makeQuery(id+"F0.imprint","IMPRINT",FACE,{"disambiguationData":[TD([[makeQuery(id+"F0.imprint","IMPRINT",EDGE,{"derivedFrom":subQ3}),1.0]])]});}
            var Q2;
            {var subQ0=sQuery(id+"F0.wireOp",EDGE,"E59");Q2=makeQuery(id+"F0.imprint","IMPRINT",FACE,{"disambiguationData":[TD([[makeQuery(id+"F0.imprint","IMPRINT",EDGE,{"derivedFrom":subQ0}),-1.0]])]});}
            var Q3;
            {var subQ1=sQuery(id+"F0.wireOp",EDGE,"E14.top");Q3=makeQuery(id+"F0.imprint","IMPRINT",FACE,{"disambiguationData":[TD([[makeQuery(id+"F0.imprint","IMPRINT",EDGE,{"derivedFrom":subQ1}),1.0]])]});}
            var Q4;
            {var subQ3=sQuery(id+"F0.wireOp",EDGE,"E35.right");Q4=makeQuery(id+"F0.imprint","IMPRINT",FACE,{"disambiguationData":[TD([[makeQuery(id+"F0.imprint","IMPRINT",EDGE,{"derivedFrom":subQ3}),-1.0]])]});}
            var Q5;
            {var subQ3=sQuery(id+"F0.wireOp",EDGE,"E52");Q5=makeQuery(id+"F0.imprint","IMPRINT",FACE,{"disambiguationData":[TD([[makeQuery(id+"F0.imprint","IMPRINT",EDGE,{"derivedFrom":subQ3}),1.0]])]});}
            var Q6;
            {var subQ7=sQuery(id+"F0.wireOp",EDGE,"E43");Q6=makeQuery(id+"F0.imprint","IMPRINT",FACE,{"disambiguationData":[TD([[makeQuery(id+"F0.imprint","IMPRINT",EDGE,{"derivedFrom":subQ7}),1.0]])]});}
            var Q7;
            Q7=makeQuery(id+"F0.imprint","IMPRINT",FACE,{"disambiguationData":[TD([[makeQuery(id+"F0.imprint","IMPRINT",EDGE,{"derivedFrom":sQuery(id+"F0.wireOp",EDGE,"E3.top")}),-1.0]])]});
            var Q8;
            {var subQ5=sQuery(id+"F0.wireOp",EDGE,"E54");Q8=makeQuery(id+"F0.imprint","IMPRINT",FACE,{"disambiguationData":[TD([[makeQuery(id+"F0.imprint","IMPRINT",EDGE,{"derivedFrom":subQ5}),-1.0]])]});}
            var Q9;
            {var subQ4=sQuery(id+"F0.wireOp",EDGE,"E53");Q9=makeQuery(id+"F0.imprint","IMPRINT",FACE,{"disambiguationData":[TD([[makeQuery(id+"F0.imprint","IMPRINT",EDGE,{"derivedFrom":subQ4}),1.0]])]});}
            var Q10;
            {var subQ0=sQuery(id+"F0.wireOp",EDGE,"E17.bottom");Q10=makeQuery(id+"F0.imprint","IMPRINT",FACE,{"disambiguationData":[TD([[makeQuery(id+"F0.imprint","IMPRINT",EDGE,{"derivedFrom":subQ0}),1.0]])]});}
            var Q11;
            {var subQ3=sQuery(id+"F0.wireOp",EDGE,"E56");Q11=makeQuery(id+"F0.imprint","IMPRINT",FACE,{"disambiguationData":[TD([[makeQuery(id+"F0.imprint","IMPRINT",EDGE,{"derivedFrom":subQ3}),1.0]])]});}
            var Q12;
            {var subQ4=sQuery(id+"F0.wireOp",EDGE,"E15.top");var subQ6=sQuery(id+"F0.wireOp",EDGE,"E15.left");var subQ7=makeQuery(id+"F0.imprint","INTERSECT",VERTEX,{"derivedFrom":[subQ4,subQ6]});Q12=makeQuery(id+"F0.imprint","IMPRINT",FACE,{"disambiguationData":[TD([[makeQuery(id+"F0.imprint","IMPRINT",EDGE,{"disambiguationData":[TD([[subQ7,-1.0]])],"derivedFrom":subQ4}),1.0]])]});}
            var Q13;
            Q13=makeQuery(id+"F0.imprint","IMPRINT",FACE,{"disambiguationData":[TD([[makeQuery(id+"F0.imprint","IMPRINT",EDGE,{"derivedFrom":sQuery(id+"F0.wireOp",EDGE,"E16.right")}),1.0]])]});
            var Q14;
            {var subQ1=sQuery(id+"F0.wireOp",EDGE,"E29.right");Q14=makeQuery(id+"F0.imprint","IMPRINT",FACE,{"disambiguationData":[TD([[makeQuery(id+"F0.imprint","IMPRINT",EDGE,{"derivedFrom":subQ1}),-1.0]])]});}
            var Q15;
            Q15=makeQuery(id+"F0.imprint","IMPRINT",FACE,{"disambiguationData":[TD([[makeQuery(id+"F0.imprint","IMPRINT",EDGE,{"derivedFrom":sQuery(id+"F0.wireOp",EDGE,"E39.top")}),-1.0]])]});
            var Q16;
            {var subQ1=sQuery(id+"F0.wireOp",EDGE,"E1.top");Q16=makeQuery(id+"F0.imprint","IMPRINT",FACE,{"disambiguationData":[TD([[makeQuery(id+"F0.imprint","IMPRINT",EDGE,{"derivedFrom":subQ1}),-1.0]])]});}
            var Q17;
            {var subQ4=sQuery(id+"F0.wireOp",EDGE,"E1.top");Q17=makeQuery(id+"F0.imprint","IMPRINT",FACE,{"disambiguationData":[TD([[makeQuery(id+"F0.imprint","IMPRINT",EDGE,{"derivedFrom":subQ4}),1.0]])]});}
            var Q18;
            {var subQ0=sQuery(id+"F0.wireOp",EDGE,"E57");Q18=makeQuery(id+"F0.imprint","IMPRINT",FACE,{"disambiguationData":[TD([[makeQuery(id+"F0.imprint","IMPRINT",EDGE,{"derivedFrom":subQ0}),-1.0]])]});}
            var Q19;
            {var subQ0=sQuery(id+"F0.wireOp",EDGE,"E57");Q19=makeQuery(id+"F0.imprint","IMPRINT",FACE,{"disambiguationData":[TD([[makeQuery(id+"F0.imprint","IMPRINT",EDGE,{"derivedFrom":subQ0}),1.0]])]});}
            var Q20;
            {var subQ0=sQuery(id+"F0.wireOp",EDGE,"E26.top");var subQ5=sQuery(id+"F0.wireOp",EDGE,"E21.trimOffspring");var subQ6=makeQuery(id+"F0.imprint","INTERSECT",VERTEX,{"derivedFrom":[subQ5,subQ0]});Q20=makeQuery(id+"F0.imprint","IMPRINT",FACE,{"disambiguationData":[TD([[makeQuery(id+"F0.imprint","IMPRINT",EDGE,{"disambiguationData":[TD([[subQ6,-1.0]])],"derivedFrom":subQ5}),1.0]])]});}
            var Q21;
            {var subQ5=sQuery(id+"F0.wireOp",EDGE,"E68");Q21=makeQuery(id+"F0.imprint","IMPRINT",FACE,{"disambiguationData":[TD([[makeQuery(id+"F0.imprint","IMPRINT",EDGE,{"derivedFrom":subQ5}),-1.0]])]});}
            var Q22;
            {var subQ0=sQuery(id+"F0.wireOp",EDGE,"E28.trimOffspring");var subQ1=sQuery(id+"F0.wireOp",EDGE,"E15.right");var subQ2=makeQuery(id+"F0.imprint","INTERSECT",VERTEX,{"derivedFrom":[subQ1,subQ0]});Q22=makeQuery(id+"F0.imprint","IMPRINT",FACE,{"disambiguationData":[TD([[makeQuery(id+"F0.imprint","IMPRINT",EDGE,{"disambiguationData":[TD([[subQ2,1.0]])],"derivedFrom":subQ1}),-1.0]])]});}
            var Q23;
            {var subQ0=sQuery(id+"F0.wireOp",EDGE,"E26.top");var subQ1=sQuery(id+"F0.wireOp",EDGE,"E21.trimOffspring");var subQ2=makeQuery(id+"F0.imprint","INTERSECT",VERTEX,{"derivedFrom":[subQ1,subQ0]});Q23=makeQuery(id+"F0.imprint","IMPRINT",FACE,{"disambiguationData":[TD([[makeQuery(id+"F0.imprint","IMPRINT",EDGE,{"disambiguationData":[TD([[subQ2,-1.0]])],"derivedFrom":subQ1}),-1.0]])]});}
            var Q24;
            {var subQ0=sQuery(id+"F0.wireOp",EDGE,"E28.trimOffspring");var subQ1=sQuery(id+"F0.wireOp",EDGE,"E21.trimOffspring");var subQ2=makeQuery(id+"F0.imprint","INTERSECT",VERTEX,{"derivedFrom":[subQ1,subQ0]});Q24=makeQuery(id+"F0.imprint","IMPRINT",FACE,{"disambiguationData":[TD([[makeQuery(id+"F0.imprint","IMPRINT",EDGE,{"disambiguationData":[TD([[subQ2,1.0]])],"derivedFrom":subQ1}),-1.0]])]});}
            var Q25;
            {var subQ1=sQuery(id+"F0.wireOp",EDGE,"E15.top");var subQ6=makeQuery(id+"F0.imprint","INTERSECT",VERTEX,{"derivedFrom":[subQ1,sQuery(id+"F0.wireOp",EDGE,"E34")]});Q25=makeQuery(id+"F0.imprint","IMPRINT",FACE,{"disambiguationData":[TD([[makeQuery(id+"F0.imprint","IMPRINT",EDGE,{"disambiguationData":[TD([[subQ6,1.0]])],"derivedFrom":subQ1}),1.0]])]});}
            var Q26;
            {var subQ4=sQuery(id+"F0.wireOp",EDGE,"E0.bottom");Q26=makeQuery(id+"F0.imprint","IMPRINT",FACE,{"disambiguationData":[TD([[makeQuery(id+"F0.imprint","IMPRINT",EDGE,{"derivedFrom":subQ4}),1.0]])]});}
            var Q27;
            {var subQ0=sQuery(id+"F0.wireOp",EDGE,"E63");Q27=makeQuery(id+"F0.imprint","IMPRINT",FACE,{"disambiguationData":[TD([[makeQuery(id+"F0.imprint","IMPRINT",EDGE,{"derivedFrom":subQ0}),-1.0]])]});}
            var Q28;
            {var subQ0=sQuery(id+"F0.wireOp",EDGE,"E31");Q28=makeQuery(id+"F0.imprint","IMPRINT",FACE,{"disambiguationData":[TD([[makeQuery(id+"F0.imprint","IMPRINT",EDGE,{"derivedFrom":subQ0}),1.0]])]});}
            var Q29;
            {var subQ0=sQuery(id+"F0.wireOp",EDGE,"E48");Q29=makeQuery(id+"F0.imprint","IMPRINT",FACE,{"disambiguationData":[TD([[makeQuery(id+"F0.imprint","IMPRINT",EDGE,{"derivedFrom":subQ0}),-1.0]])]});}
            var Q30;
            {var subQ5=sQuery(id+"F0.wireOp",EDGE,"E49");Q30=makeQuery(id+"F0.imprint","IMPRINT",FACE,{"disambiguationData":[TD([[makeQuery(id+"F0.imprint","IMPRINT",EDGE,{"derivedFrom":subQ5}),1.0]])]});}
            var Q31;
            {var subQ2=sQuery(id+"F0.wireOp",EDGE,"E6.top");Q31=makeQuery(id+"F0.imprint","IMPRINT",FACE,{"disambiguationData":[TD([[makeQuery(id+"F0.imprint","IMPRINT",EDGE,{"derivedFrom":subQ2}),1.0]])]});}
            var Q32;
            {var subQ0=sQuery(id+"F0.wireOp",EDGE,"E24.trimOffspring");Q32=makeQuery(id+"F0.imprint","IMPRINT",FACE,{"disambiguationData":[TD([[makeQuery(id+"F0.imprint","IMPRINT",EDGE,{"derivedFrom":subQ0}),-1.0]])]});}
            var Q33;
            {var subQ0=sQuery(id+"F0.wireOp",EDGE,"E66");Q33=makeQuery(id+"F0.imprint","IMPRINT",FACE,{"disambiguationData":[TD([[makeQuery(id+"F0.imprint","IMPRINT",EDGE,{"derivedFrom":subQ0}),-1.0]])]});}
            var Q34;
            Q34=makeQuery(id+"F2.opExtrude","CAP_FACE",FACE,{"disambiguationData":[OSD([sQuery(id+"F0.wireOp",EDGE,"E3.top"),sQuery(id+"F0.wireOp",EDGE,"E4.left"),sQuery(id+"F0.wireOp",EDGE,"E4.right"),sQuery(id+"F0.wireOp",EDGE,"E5.left"),sQuery(id+"F0.wireOp",EDGE,"E5.right"),sQuery(id+"F0.wireOp",EDGE,"E6.top"),sQuery(id+"F0.wireOp",EDGE,"E6.left"),sQuery(id+"F0.wireOp",EDGE,"E6.right"),sQuery(id+"F0.wireOp",EDGE,"E7"),sQuery(id+"F0.wireOp",EDGE,"E8.trimOffspring"),sQuery(id+"F0.wireOp",EDGE,"E11.trimOffspring"),sQuery(id+"F0.wireOp",EDGE,"E13.bottom"),sQuery(id+"F0.wireOp",EDGE,"E13.top"),sQuery(id+"F0.wireOp",EDGE,"E13.left"),sQuery(id+"F0.wireOp",EDGE,"E14.bottom"),sQuery(id+"F0.wireOp",EDGE,"E14.top"),sQuery(id+"F0.wireOp",EDGE,"E14.left"),sQuery(id+"F0.wireOp",EDGE,"E15.bottom"),sQuery(id+"F0.wireOp",EDGE,"E15.left"),sQuery(id+"F0.wireOp",EDGE,"E20.bottom"),sQuery(id+"F0.wireOp",EDGE,"E20.top"),sQuery(id+"F0.wireOp",EDGE,"E19.right"),sQuery(id+"F0.wireOp",EDGE,"E22.trimOffspring"),sQuery(id+"F0.wireOp",EDGE,"E23.trimOffspring"),sQuery(id+"F0.wireOp",EDGE,"E5.bottom"),sQuery(id+"F0.wireOp",EDGE,"E35.top"),sQuery(id+"F0.wireOp",EDGE,"E35.right"),sQuery(id+"F0.wireOp",EDGE,"E36.bottom"),sQuery(id+"F0.wireOp",EDGE,"E36.top"),sQuery(id+"F0.wireOp",EDGE,"E36.left"),sQuery(id+"F0.wireOp",EDGE,"E36.right"),sQuery(id+"F0.wireOp",EDGE,"E48"),sQuery(id+"F0.wireOp",EDGE,"E49"),sQuery(id+"F0.wireOp",EDGE,"E51"),sQuery(id+"F0.wireOp",EDGE,"E52"),sQuery(id+"F0.wireOp",EDGE,"E54"),sQuery(id+"F0.wireOp",EDGE,"E66"),sQuery(id+"F0.wireOp",EDGE,"E67")])],"isStart":false});
            extrude(context, id + "F3", {"entities" : qUnion([Q0, Q1, Q2, Q3, Q4, Q5, Q6, Q7, Q8, Q9, Q10, Q11, Q12, Q13, Q14, Q15, Q16, Q17, Q18, Q19, Q20, Q21, Q22, Q23, Q24, Q25, Q26, Q27, Q28, Q29, Q30, Q31, Q32, Q33]), "depth" : 1500 * mm, "hasSecondDirection" : true, "secondDirectionOppositeDirection" : false, "secondDirectionBoundEntityFace" : qUnion([Q34]), "secondDirectionDepth" : 1000 * mm});
        }
        {
            var Q0;
            {var subQ1=sQuery(id+"F0.wireOp",EDGE,"E14.top");Q0=makeQuery(id+"F0.imprint","IMPRINT",FACE,{"disambiguationData":[TD([[makeQuery(id+"F0.imprint","IMPRINT",EDGE,{"derivedFrom":subQ1}),1.0]])]});}
            var Q1;
            {var subQ3=sQuery(id+"F0.wireOp",EDGE,"E59");Q1=makeQuery(id+"F0.imprint","IMPRINT",FACE,{"disambiguationData":[TD([[makeQuery(id+"F0.imprint","IMPRINT",EDGE,{"derivedFrom":subQ3}),1.0]])]});}
            var Q2;
            {var subQ2=sQuery(id+"F0.wireOp",EDGE,"E20.bottom");Q2=makeQuery(id+"F0.imprint","IMPRINT",FACE,{"disambiguationData":[TD([[makeQuery(id+"F0.imprint","IMPRINT",EDGE,{"derivedFrom":subQ2}),1.0]])]});}
            var Q3;
            {var subQ3=sQuery(id+"F0.wireOp",EDGE,"E35.right");Q3=makeQuery(id+"F0.imprint","IMPRINT",FACE,{"disambiguationData":[TD([[makeQuery(id+"F0.imprint","IMPRINT",EDGE,{"derivedFrom":subQ3}),-1.0]])]});}
            var Q4;
            {var subQ3=sQuery(id+"F0.wireOp",EDGE,"E52");Q4=makeQuery(id+"F0.imprint","IMPRINT",FACE,{"disambiguationData":[TD([[makeQuery(id+"F0.imprint","IMPRINT",EDGE,{"derivedFrom":subQ3}),1.0]])]});}
            var Q5;
            {var subQ7=sQuery(id+"F0.wireOp",EDGE,"E43");Q5=makeQuery(id+"F0.imprint","IMPRINT",FACE,{"disambiguationData":[TD([[makeQuery(id+"F0.imprint","IMPRINT",EDGE,{"derivedFrom":subQ7}),1.0]])]});}
            var Q6;
            {var subQ5=sQuery(id+"F0.wireOp",EDGE,"E49");Q6=makeQuery(id+"F0.imprint","IMPRINT",FACE,{"disambiguationData":[TD([[makeQuery(id+"F0.imprint","IMPRINT",EDGE,{"derivedFrom":subQ5}),1.0]])]});}
            var Q7;
            {var subQ0=sQuery(id+"F0.wireOp",EDGE,"E48");Q7=makeQuery(id+"F0.imprint","IMPRINT",FACE,{"disambiguationData":[TD([[makeQuery(id+"F0.imprint","IMPRINT",EDGE,{"derivedFrom":subQ0}),-1.0]])]});}
            var Q8;
            {var subQ5=sQuery(id+"F0.wireOp",EDGE,"E54");Q8=makeQuery(id+"F0.imprint","IMPRINT",FACE,{"disambiguationData":[TD([[makeQuery(id+"F0.imprint","IMPRINT",EDGE,{"derivedFrom":subQ5}),-1.0]])]});}
            var Q9;
            {var subQ4=sQuery(id+"F0.wireOp",EDGE,"E53");Q9=makeQuery(id+"F0.imprint","IMPRINT",FACE,{"disambiguationData":[TD([[makeQuery(id+"F0.imprint","IMPRINT",EDGE,{"derivedFrom":subQ4}),1.0]])]});}
            var Q10;
            {var subQ0=sQuery(id+"F0.wireOp",EDGE,"E17.bottom");Q10=makeQuery(id+"F0.imprint","IMPRINT",FACE,{"disambiguationData":[TD([[makeQuery(id+"F0.imprint","IMPRINT",EDGE,{"derivedFrom":subQ0}),1.0]])]});}
            var Q11;
            Q11=makeQuery(id+"F0.imprint","IMPRINT",FACE,{"disambiguationData":[TD([[makeQuery(id+"F0.imprint","IMPRINT",EDGE,{"derivedFrom":sQuery(id+"F0.wireOp",EDGE,"E16.right")}),1.0]])]});
            var Q12;
            {var subQ1=sQuery(id+"F0.wireOp",EDGE,"E29.right");Q12=makeQuery(id+"F0.imprint","IMPRINT",FACE,{"disambiguationData":[TD([[makeQuery(id+"F0.imprint","IMPRINT",EDGE,{"derivedFrom":subQ1}),-1.0]])]});}
            var Q13;
            Q13=makeQuery(id+"F0.imprint","IMPRINT",FACE,{"disambiguationData":[TD([[makeQuery(id+"F0.imprint","IMPRINT",EDGE,{"derivedFrom":sQuery(id+"F0.wireOp",EDGE,"E39.top")}),-1.0]])]});
            var Q14;
            {var subQ1=sQuery(id+"F0.wireOp",EDGE,"E1.top");Q14=makeQuery(id+"F0.imprint","IMPRINT",FACE,{"disambiguationData":[TD([[makeQuery(id+"F0.imprint","IMPRINT",EDGE,{"derivedFrom":subQ1}),-1.0]])]});}
            var Q15;
            {var subQ4=sQuery(id+"F0.wireOp",EDGE,"E1.top");Q15=makeQuery(id+"F0.imprint","IMPRINT",FACE,{"disambiguationData":[TD([[makeQuery(id+"F0.imprint","IMPRINT",EDGE,{"derivedFrom":subQ4}),1.0]])]});}
            var Q16;
            {var subQ3=sQuery(id+"F0.wireOp",EDGE,"E56");Q16=makeQuery(id+"F0.imprint","IMPRINT",FACE,{"disambiguationData":[TD([[makeQuery(id+"F0.imprint","IMPRINT",EDGE,{"derivedFrom":subQ3}),1.0]])]});}
            var Q17;
            {var subQ4=sQuery(id+"F0.wireOp",EDGE,"E15.top");var subQ6=sQuery(id+"F0.wireOp",EDGE,"E15.left");var subQ7=makeQuery(id+"F0.imprint","INTERSECT",VERTEX,{"derivedFrom":[subQ4,subQ6]});Q17=makeQuery(id+"F0.imprint","IMPRINT",FACE,{"disambiguationData":[TD([[makeQuery(id+"F0.imprint","IMPRINT",EDGE,{"disambiguationData":[TD([[subQ7,-1.0]])],"derivedFrom":subQ4}),1.0]])]});}
            var Q18;
            {var subQ1=sQuery(id+"F0.wireOp",EDGE,"E15.top");var subQ6=makeQuery(id+"F0.imprint","INTERSECT",VERTEX,{"derivedFrom":[subQ1,sQuery(id+"F0.wireOp",EDGE,"E34")]});Q18=makeQuery(id+"F0.imprint","IMPRINT",FACE,{"disambiguationData":[TD([[makeQuery(id+"F0.imprint","IMPRINT",EDGE,{"disambiguationData":[TD([[subQ6,1.0]])],"derivedFrom":subQ1}),1.0]])]});}
            var Q19;
            {var subQ0=sQuery(id+"F0.wireOp",EDGE,"E28.trimOffspring");var subQ1=sQuery(id+"F0.wireOp",EDGE,"E15.right");var subQ2=makeQuery(id+"F0.imprint","INTERSECT",VERTEX,{"derivedFrom":[subQ1,subQ0]});Q19=makeQuery(id+"F0.imprint","IMPRINT",FACE,{"disambiguationData":[TD([[makeQuery(id+"F0.imprint","IMPRINT",EDGE,{"disambiguationData":[TD([[subQ2,1.0]])],"derivedFrom":subQ1}),-1.0]])]});}
            var Q20;
            {var subQ0=sQuery(id+"F0.wireOp",EDGE,"E28.trimOffspring");var subQ1=sQuery(id+"F0.wireOp",EDGE,"E21.trimOffspring");var subQ2=makeQuery(id+"F0.imprint","INTERSECT",VERTEX,{"derivedFrom":[subQ1,subQ0]});Q20=makeQuery(id+"F0.imprint","IMPRINT",FACE,{"disambiguationData":[TD([[makeQuery(id+"F0.imprint","IMPRINT",EDGE,{"disambiguationData":[TD([[subQ2,1.0]])],"derivedFrom":subQ1}),-1.0]])]});}
            var Q21;
            {var subQ0=sQuery(id+"F0.wireOp",EDGE,"E26.top");var subQ1=sQuery(id+"F0.wireOp",EDGE,"E21.trimOffspring");var subQ2=makeQuery(id+"F0.imprint","INTERSECT",VERTEX,{"derivedFrom":[subQ1,subQ0]});Q21=makeQuery(id+"F0.imprint","IMPRINT",FACE,{"disambiguationData":[TD([[makeQuery(id+"F0.imprint","IMPRINT",EDGE,{"disambiguationData":[TD([[subQ2,-1.0]])],"derivedFrom":subQ1}),-1.0]])]});}
            var Q22;
            {var subQ0=sQuery(id+"F0.wireOp",EDGE,"E26.top");var subQ5=sQuery(id+"F0.wireOp",EDGE,"E21.trimOffspring");var subQ6=makeQuery(id+"F0.imprint","INTERSECT",VERTEX,{"derivedFrom":[subQ5,subQ0]});Q22=makeQuery(id+"F0.imprint","IMPRINT",FACE,{"disambiguationData":[TD([[makeQuery(id+"F0.imprint","IMPRINT",EDGE,{"disambiguationData":[TD([[subQ6,-1.0]])],"derivedFrom":subQ5}),1.0]])]});}
            var Q23;
            {var subQ0=sQuery(id+"F0.wireOp",EDGE,"E57");Q23=makeQuery(id+"F0.imprint","IMPRINT",FACE,{"disambiguationData":[TD([[makeQuery(id+"F0.imprint","IMPRINT",EDGE,{"derivedFrom":subQ0}),1.0]])]});}
            var Q24;
            {var subQ5=sQuery(id+"F0.wireOp",EDGE,"E68");Q24=makeQuery(id+"F0.imprint","IMPRINT",FACE,{"disambiguationData":[TD([[makeQuery(id+"F0.imprint","IMPRINT",EDGE,{"derivedFrom":subQ5}),-1.0]])]});}
            var Q25;
            {var subQ0=sQuery(id+"F0.wireOp",EDGE,"E31");Q25=makeQuery(id+"F0.imprint","IMPRINT",FACE,{"disambiguationData":[TD([[makeQuery(id+"F0.imprint","IMPRINT",EDGE,{"derivedFrom":subQ0}),1.0]])]});}
            var Q26;
            {var subQ0=sQuery(id+"F0.wireOp",EDGE,"E63");Q26=makeQuery(id+"F0.imprint","IMPRINT",FACE,{"disambiguationData":[TD([[makeQuery(id+"F0.imprint","IMPRINT",EDGE,{"derivedFrom":subQ0}),-1.0]])]});}
            var Q27;
            {var subQ4=sQuery(id+"F0.wireOp",EDGE,"E0.bottom");Q27=makeQuery(id+"F0.imprint","IMPRINT",FACE,{"disambiguationData":[TD([[makeQuery(id+"F0.imprint","IMPRINT",EDGE,{"derivedFrom":subQ4}),1.0]])]});}
            var Q28;
            Q28=makeQuery(id+"F0.imprint","IMPRINT",FACE,{"disambiguationData":[TD([[makeQuery(id+"F0.imprint","IMPRINT",EDGE,{"derivedFrom":sQuery(id+"F0.wireOp",EDGE,"E3.top")}),-1.0]])]});
            var Q29;
            {var subQ2=sQuery(id+"F0.wireOp",EDGE,"E6.top");Q29=makeQuery(id+"F0.imprint","IMPRINT",FACE,{"disambiguationData":[TD([[makeQuery(id+"F0.imprint","IMPRINT",EDGE,{"derivedFrom":subQ2}),1.0]])]});}
            var Q30;
            {var subQ0=sQuery(id+"F0.wireOp",EDGE,"E24.trimOffspring");Q30=makeQuery(id+"F0.imprint","IMPRINT",FACE,{"disambiguationData":[TD([[makeQuery(id+"F0.imprint","IMPRINT",EDGE,{"derivedFrom":subQ0}),-1.0]])]});}
            var Q31;
            {var subQ0=sQuery(id+"F0.wireOp",EDGE,"E66");Q31=makeQuery(id+"F0.imprint","IMPRINT",FACE,{"disambiguationData":[TD([[makeQuery(id+"F0.imprint","IMPRINT",EDGE,{"derivedFrom":subQ0}),-1.0]])]});}
            var Q32;
            Q32=makeQuery(id+"F2.opExtrude","CAP_FACE",FACE,{"disambiguationData":[OSD([sQuery(id+"F0.wireOp",EDGE,"E3.top"),sQuery(id+"F0.wireOp",EDGE,"E4.left"),sQuery(id+"F0.wireOp",EDGE,"E4.right"),sQuery(id+"F0.wireOp",EDGE,"E5.left"),sQuery(id+"F0.wireOp",EDGE,"E5.right"),sQuery(id+"F0.wireOp",EDGE,"E6.right"),sQuery(id+"F0.wireOp",EDGE,"E8.trimOffspring"),sQuery(id+"F0.wireOp",EDGE,"E11.trimOffspring"),sQuery(id+"F0.wireOp",EDGE,"E13.bottom"),sQuery(id+"F0.wireOp",EDGE,"E13.top"),sQuery(id+"F0.wireOp",EDGE,"E13.left"),sQuery(id+"F0.wireOp",EDGE,"E14.bottom"),sQuery(id+"F0.wireOp",EDGE,"E14.top"),sQuery(id+"F0.wireOp",EDGE,"E14.left"),sQuery(id+"F0.wireOp",EDGE,"E15.bottom"),sQuery(id+"F0.wireOp",EDGE,"E15.left"),sQuery(id+"F0.wireOp",EDGE,"E20.bottom"),sQuery(id+"F0.wireOp",EDGE,"E20.top"),sQuery(id+"F0.wireOp",EDGE,"E19.right"),sQuery(id+"F0.wireOp",EDGE,"E22.trimOffspring"),sQuery(id+"F0.wireOp",EDGE,"E23.trimOffspring"),sQuery(id+"F0.wireOp",EDGE,"E35.top"),sQuery(id+"F0.wireOp",EDGE,"E35.right"),sQuery(id+"F0.wireOp",EDGE,"E36.bottom"),sQuery(id+"F0.wireOp",EDGE,"E36.top"),sQuery(id+"F0.wireOp",EDGE,"E36.left"),sQuery(id+"F0.wireOp",EDGE,"E36.right"),sQuery(id+"F0.wireOp",EDGE,"E37"),sQuery(id+"F0.wireOp",EDGE,"E48"),sQuery(id+"F0.wireOp",EDGE,"E51"),sQuery(id+"F0.wireOp",EDGE,"E52"),sQuery(id+"F0.wireOp",EDGE,"E54")])],"isStart":false});
            extrude(context, id + "F4", {"entities" : qUnion([Q0, Q1, Q2, Q3, Q4, Q5, Q6, Q7, Q8, Q9, Q10, Q11, Q12, Q13, Q14, Q15, Q16, Q17, Q18, Q19, Q20, Q21, Q22, Q23, Q24, Q25, Q26, Q27, Q28, Q29, Q30, Q31]), "depth" : 2000 * mm, "hasSecondDirection" : true, "secondDirectionOppositeDirection" : false, "secondDirectionBoundEntityFace" : qUnion([Q32]), "secondDirectionDepth" : 1500 * mm});
        }
        {
            var Q0;
            {var subQ1=sQuery(id+"F0.wireOp",EDGE,"E14.top");Q0=makeQuery(id+"F0.imprint","IMPRINT",FACE,{"disambiguationData":[TD([[makeQuery(id+"F0.imprint","IMPRINT",EDGE,{"derivedFrom":subQ1}),1.0]])]});}
            var Q1;
            {var subQ3=sQuery(id+"F0.wireOp",EDGE,"E35.right");Q1=makeQuery(id+"F0.imprint","IMPRINT",FACE,{"disambiguationData":[TD([[makeQuery(id+"F0.imprint","IMPRINT",EDGE,{"derivedFrom":subQ3}),-1.0]])]});}
            var Q2;
            {var subQ0=sQuery(id+"F0.wireOp",EDGE,"E59");Q2=makeQuery(id+"F0.imprint","IMPRINT",FACE,{"disambiguationData":[TD([[makeQuery(id+"F0.imprint","IMPRINT",EDGE,{"derivedFrom":subQ0}),-1.0]])]});}
            var Q3;
            {var subQ3=sQuery(id+"F0.wireOp",EDGE,"E59");Q3=makeQuery(id+"F0.imprint","IMPRINT",FACE,{"disambiguationData":[TD([[makeQuery(id+"F0.imprint","IMPRINT",EDGE,{"derivedFrom":subQ3}),1.0]])]});}
            var Q4;
            {var subQ2=sQuery(id+"F0.wireOp",EDGE,"E20.bottom");Q4=makeQuery(id+"F0.imprint","IMPRINT",FACE,{"disambiguationData":[TD([[makeQuery(id+"F0.imprint","IMPRINT",EDGE,{"derivedFrom":subQ2}),1.0]])]});}
            var Q5;
            {var subQ0=sQuery(id+"F0.wireOp",EDGE,"E42");Q5=makeQuery(id+"F0.imprint","IMPRINT",FACE,{"disambiguationData":[TD([[makeQuery(id+"F0.imprint","IMPRINT",EDGE,{"derivedFrom":subQ0}),1.0]])]});}
            var Q6;
            {var subQ7=sQuery(id+"F0.wireOp",EDGE,"E43");Q6=makeQuery(id+"F0.imprint","IMPRINT",FACE,{"disambiguationData":[TD([[makeQuery(id+"F0.imprint","IMPRINT",EDGE,{"derivedFrom":subQ7}),1.0]])]});}
            var Q7;
            {var subQ0=sQuery(id+"F0.wireOp",EDGE,"E44");Q7=makeQuery(id+"F0.imprint","IMPRINT",FACE,{"disambiguationData":[TD([[makeQuery(id+"F0.imprint","IMPRINT",EDGE,{"derivedFrom":subQ0}),-1.0]])]});}
            var Q8;
            Q8=makeQuery(id+"F0.imprint","IMPRINT",FACE,{"disambiguationData":[TD([[makeQuery(id+"F0.imprint","IMPRINT",EDGE,{"derivedFrom":sQuery(id+"F0.wireOp",EDGE,"E3.top")}),-1.0]])]});
            var Q9;
            {var subQ5=sQuery(id+"F0.wireOp",EDGE,"E49");Q9=makeQuery(id+"F0.imprint","IMPRINT",FACE,{"disambiguationData":[TD([[makeQuery(id+"F0.imprint","IMPRINT",EDGE,{"derivedFrom":subQ5}),1.0]])]});}
            var Q10;
            {var subQ0=sQuery(id+"F0.wireOp",EDGE,"E48");Q10=makeQuery(id+"F0.imprint","IMPRINT",FACE,{"disambiguationData":[TD([[makeQuery(id+"F0.imprint","IMPRINT",EDGE,{"derivedFrom":subQ0}),1.0]])]});}
            var Q11;
            {var subQ0=sQuery(id+"F0.wireOp",EDGE,"E48");Q11=makeQuery(id+"F0.imprint","IMPRINT",FACE,{"disambiguationData":[TD([[makeQuery(id+"F0.imprint","IMPRINT",EDGE,{"derivedFrom":subQ0}),-1.0]])]});}
            var Q12;
            {var subQ0=sQuery(id+"F0.wireOp",EDGE,"E51");Q12=makeQuery(id+"F0.imprint","IMPRINT",FACE,{"disambiguationData":[TD([[makeQuery(id+"F0.imprint","IMPRINT",EDGE,{"derivedFrom":subQ0}),1.0]])]});}
            var Q13;
            {var subQ3=sQuery(id+"F0.wireOp",EDGE,"E52");Q13=makeQuery(id+"F0.imprint","IMPRINT",FACE,{"disambiguationData":[TD([[makeQuery(id+"F0.imprint","IMPRINT",EDGE,{"derivedFrom":subQ3}),1.0]])]});}
            var Q14;
            {var subQ4=sQuery(id+"F0.wireOp",EDGE,"E0.bottom");Q14=makeQuery(id+"F0.imprint","IMPRINT",FACE,{"disambiguationData":[TD([[makeQuery(id+"F0.imprint","IMPRINT",EDGE,{"derivedFrom":subQ4}),1.0]])]});}
            var Q15;
            {var subQ4=sQuery(id+"F0.wireOp",EDGE,"E1.top");Q15=makeQuery(id+"F0.imprint","IMPRINT",FACE,{"disambiguationData":[TD([[makeQuery(id+"F0.imprint","IMPRINT",EDGE,{"derivedFrom":subQ4}),1.0]])]});}
            var Q16;
            {var subQ0=sQuery(id+"F0.wireOp",EDGE,"E63");Q16=makeQuery(id+"F0.imprint","IMPRINT",FACE,{"disambiguationData":[TD([[makeQuery(id+"F0.imprint","IMPRINT",EDGE,{"derivedFrom":subQ0}),-1.0]])]});}
            var Q17;
            {var subQ0=sQuery(id+"F0.wireOp",EDGE,"E63");Q17=makeQuery(id+"F0.imprint","IMPRINT",FACE,{"disambiguationData":[TD([[makeQuery(id+"F0.imprint","IMPRINT",EDGE,{"derivedFrom":subQ0}),1.0]])]});}
            var Q18;
            {var subQ1=sQuery(id+"F0.wireOp",EDGE,"E1.top");Q18=makeQuery(id+"F0.imprint","IMPRINT",FACE,{"disambiguationData":[TD([[makeQuery(id+"F0.imprint","IMPRINT",EDGE,{"derivedFrom":subQ1}),-1.0]])]});}
            var Q19;
            {var subQ0=sQuery(id+"F0.wireOp",EDGE,"E68");Q19=makeQuery(id+"F0.imprint","IMPRINT",FACE,{"disambiguationData":[TD([[makeQuery(id+"F0.imprint","IMPRINT",EDGE,{"derivedFrom":subQ0}),1.0]])]});}
            var Q20;
            {var subQ5=sQuery(id+"F0.wireOp",EDGE,"E68");Q20=makeQuery(id+"F0.imprint","IMPRINT",FACE,{"disambiguationData":[TD([[makeQuery(id+"F0.imprint","IMPRINT",EDGE,{"derivedFrom":subQ5}),-1.0]])]});}
            var Q21;
            {var subQ0=sQuery(id+"F0.wireOp",EDGE,"E26.top");var subQ5=sQuery(id+"F0.wireOp",EDGE,"E21.trimOffspring");var subQ6=makeQuery(id+"F0.imprint","INTERSECT",VERTEX,{"derivedFrom":[subQ5,subQ0]});Q21=makeQuery(id+"F0.imprint","IMPRINT",FACE,{"disambiguationData":[TD([[makeQuery(id+"F0.imprint","IMPRINT",EDGE,{"disambiguationData":[TD([[subQ6,-1.0]])],"derivedFrom":subQ5}),1.0]])]});}
            var Q22;
            {var subQ0=sQuery(id+"F0.wireOp",EDGE,"E28.trimOffspring");var subQ1=sQuery(id+"F0.wireOp",EDGE,"E15.right");var subQ2=makeQuery(id+"F0.imprint","INTERSECT",VERTEX,{"derivedFrom":[subQ1,subQ0]});Q22=makeQuery(id+"F0.imprint","IMPRINT",FACE,{"disambiguationData":[TD([[makeQuery(id+"F0.imprint","IMPRINT",EDGE,{"disambiguationData":[TD([[subQ2,1.0]])],"derivedFrom":subQ1}),-1.0]])]});}
            var Q23;
            {var subQ1=sQuery(id+"F0.wireOp",EDGE,"E15.top");var subQ6=makeQuery(id+"F0.imprint","INTERSECT",VERTEX,{"derivedFrom":[subQ1,sQuery(id+"F0.wireOp",EDGE,"E34")]});Q23=makeQuery(id+"F0.imprint","IMPRINT",FACE,{"disambiguationData":[TD([[makeQuery(id+"F0.imprint","IMPRINT",EDGE,{"disambiguationData":[TD([[subQ6,1.0]])],"derivedFrom":subQ1}),1.0]])]});}
            var Q24;
            {var subQ0=sQuery(id+"F0.wireOp",EDGE,"E26.top");var subQ1=sQuery(id+"F0.wireOp",EDGE,"E21.trimOffspring");var subQ2=makeQuery(id+"F0.imprint","INTERSECT",VERTEX,{"derivedFrom":[subQ1,subQ0]});Q24=makeQuery(id+"F0.imprint","IMPRINT",FACE,{"disambiguationData":[TD([[makeQuery(id+"F0.imprint","IMPRINT",EDGE,{"disambiguationData":[TD([[subQ2,-1.0]])],"derivedFrom":subQ1}),-1.0]])]});}
            var Q25;
            {var subQ0=sQuery(id+"F0.wireOp",EDGE,"E31");Q25=makeQuery(id+"F0.imprint","IMPRINT",FACE,{"disambiguationData":[TD([[makeQuery(id+"F0.imprint","IMPRINT",EDGE,{"derivedFrom":subQ0}),1.0]])]});}
            var Q26;
            {var subQ0=sQuery(id+"F0.wireOp",EDGE,"E28.trimOffspring");var subQ1=sQuery(id+"F0.wireOp",EDGE,"E21.trimOffspring");var subQ2=makeQuery(id+"F0.imprint","INTERSECT",VERTEX,{"derivedFrom":[subQ1,subQ0]});Q26=makeQuery(id+"F0.imprint","IMPRINT",FACE,{"disambiguationData":[TD([[makeQuery(id+"F0.imprint","IMPRINT",EDGE,{"disambiguationData":[TD([[subQ2,1.0]])],"derivedFrom":subQ1}),-1.0]])]});}
            var Q27;
            Q27=makeQuery(id+"F0.imprint","IMPRINT",FACE,{"disambiguationData":[TD([[makeQuery(id+"F0.imprint","IMPRINT",EDGE,{"derivedFrom":sQuery(id+"F0.wireOp",EDGE,"E39.top")}),-1.0]])]});
            var Q28;
            {var subQ1=sQuery(id+"F0.wireOp",EDGE,"E29.right");Q28=makeQuery(id+"F0.imprint","IMPRINT",FACE,{"disambiguationData":[TD([[makeQuery(id+"F0.imprint","IMPRINT",EDGE,{"derivedFrom":subQ1}),-1.0]])]});}
            var Q29;
            Q29=makeQuery(id+"F0.imprint","IMPRINT",FACE,{"disambiguationData":[TD([[makeQuery(id+"F0.imprint","IMPRINT",EDGE,{"derivedFrom":sQuery(id+"F0.wireOp",EDGE,"E16.right")}),1.0]])]});
            var Q30;
            {var subQ0=sQuery(id+"F0.wireOp",EDGE,"E57");Q30=makeQuery(id+"F0.imprint","IMPRINT",FACE,{"disambiguationData":[TD([[makeQuery(id+"F0.imprint","IMPRINT",EDGE,{"derivedFrom":subQ0}),-1.0]])]});}
            var Q31;
            {var subQ0=sQuery(id+"F0.wireOp",EDGE,"E57");Q31=makeQuery(id+"F0.imprint","IMPRINT",FACE,{"disambiguationData":[TD([[makeQuery(id+"F0.imprint","IMPRINT",EDGE,{"derivedFrom":subQ0}),1.0]])]});}
            var Q32;
            {var subQ0=sQuery(id+"F0.wireOp",EDGE,"E29.top");Q32=makeQuery(id+"F0.imprint","IMPRINT",FACE,{"disambiguationData":[TD([[makeQuery(id+"F0.imprint","IMPRINT",EDGE,{"derivedFrom":subQ0}),1.0]])]});}
            var Q33;
            Q33=makeQuery(id+"F0.imprint","IMPRINT",FACE,{"disambiguationData":[TD([[makeQuery(id+"F0.imprint","IMPRINT",EDGE,{"derivedFrom":sQuery(id+"F0.wireOp",EDGE,"E2.top")}),-1.0]])]});
            var Q34;
            Q34=makeQuery(id+"F0.imprint","IMPRINT",FACE,{"disambiguationData":[TD([[makeQuery(id+"F0.imprint","IMPRINT",EDGE,{"derivedFrom":sQuery(id+"F0.wireOp",EDGE,"E19.bottom")}),1.0]])]});
            var Q35;
            {var subQ5=sQuery(id+"F0.wireOp",EDGE,"E54");Q35=makeQuery(id+"F0.imprint","IMPRINT",FACE,{"disambiguationData":[TD([[makeQuery(id+"F0.imprint","IMPRINT",EDGE,{"derivedFrom":subQ5}),-1.0]])]});}
            var Q36;
            {var subQ0=sQuery(id+"F0.wireOp",EDGE,"E53");Q36=makeQuery(id+"F0.imprint","IMPRINT",FACE,{"disambiguationData":[TD([[makeQuery(id+"F0.imprint","IMPRINT",EDGE,{"derivedFrom":subQ0}),-1.0]])]});}
            var Q37;
            {var subQ4=sQuery(id+"F0.wireOp",EDGE,"E53");Q37=makeQuery(id+"F0.imprint","IMPRINT",FACE,{"disambiguationData":[TD([[makeQuery(id+"F0.imprint","IMPRINT",EDGE,{"derivedFrom":subQ4}),1.0]])]});}
            var Q38;
            {var subQ0=sQuery(id+"F0.wireOp",EDGE,"E55");Q38=makeQuery(id+"F0.imprint","IMPRINT",FACE,{"disambiguationData":[TD([[makeQuery(id+"F0.imprint","IMPRINT",EDGE,{"derivedFrom":subQ0}),1.0]])]});}
            var Q39;
            {var subQ3=sQuery(id+"F0.wireOp",EDGE,"E56");Q39=makeQuery(id+"F0.imprint","IMPRINT",FACE,{"disambiguationData":[TD([[makeQuery(id+"F0.imprint","IMPRINT",EDGE,{"derivedFrom":subQ3}),1.0]])]});}
            var Q40;
            {var subQ4=sQuery(id+"F0.wireOp",EDGE,"E15.top");var subQ6=sQuery(id+"F0.wireOp",EDGE,"E15.left");var subQ7=makeQuery(id+"F0.imprint","INTERSECT",VERTEX,{"derivedFrom":[subQ4,subQ6]});Q40=makeQuery(id+"F0.imprint","IMPRINT",FACE,{"disambiguationData":[TD([[makeQuery(id+"F0.imprint","IMPRINT",EDGE,{"disambiguationData":[TD([[subQ7,-1.0]])],"derivedFrom":subQ4}),1.0]])]});}
            var Q41;
            {var subQ2=sQuery(id+"F0.wireOp",EDGE,"E6.top");Q41=makeQuery(id+"F0.imprint","IMPRINT",FACE,{"disambiguationData":[TD([[makeQuery(id+"F0.imprint","IMPRINT",EDGE,{"derivedFrom":subQ2}),1.0]])]});}
            var Q42;
            {var subQ0=sQuery(id+"F0.wireOp",EDGE,"E24.trimOffspring");Q42=makeQuery(id+"F0.imprint","IMPRINT",FACE,{"disambiguationData":[TD([[makeQuery(id+"F0.imprint","IMPRINT",EDGE,{"derivedFrom":subQ0}),-1.0]])]});}
            var Q43;
            {var subQ0=sQuery(id+"F0.wireOp",EDGE,"E66");Q43=makeQuery(id+"F0.imprint","IMPRINT",FACE,{"disambiguationData":[TD([[makeQuery(id+"F0.imprint","IMPRINT",EDGE,{"derivedFrom":subQ0}),1.0]])]});}
            var Q44;
            {var subQ0=sQuery(id+"F0.wireOp",EDGE,"E66");Q44=makeQuery(id+"F0.imprint","IMPRINT",FACE,{"disambiguationData":[TD([[makeQuery(id+"F0.imprint","IMPRINT",EDGE,{"derivedFrom":subQ0}),-1.0]])]});}
            extrude(context, id + "F5", {"entities" : qUnion([Q0, Q1, Q2, Q3, Q4, Q5, Q6, Q7, Q8, Q9, Q10, Q11, Q12, Q13, Q14, Q15, Q16, Q17, Q18, Q19, Q20, Q21, Q22, Q23, Q24, Q25, Q26, Q27, Q28, Q29, Q30, Q31, Q32, Q33, Q34, Q35, Q36, Q37, Q38, Q39, Q40, Q41, Q42, Q43, Q44]), "depth" : 2500 * mm, "hasSecondDirection" : true, "secondDirectionOppositeDirection" : false, "secondDirectionDepth" : 2000 * mm});
        }
        {
            var Q0;
            {var subQ1=sQuery(id+"F0.wireOp",EDGE,"E0.right");Q0=makeQuery(id+"F0.imprint","IMPRINT",FACE,{"disambiguationData":[TD([[makeQuery(id+"F0.imprint","IMPRINT",EDGE,{"derivedFrom":subQ1}),1.0]])]});}
            var Q1;
            {var subQ4=sQuery(id+"F0.wireOp",EDGE,"E16.bottom");Q1=makeQuery(id+"F0.imprint","IMPRINT",FACE,{"disambiguationData":[TD([[makeQuery(id+"F0.imprint","IMPRINT",EDGE,{"derivedFrom":subQ4}),1.0]])]});}
            extrude(context, id + "F6", {"entities" : qUnion([Q0, Q1]), "depth" : 1000 * mm});
        }
    });
